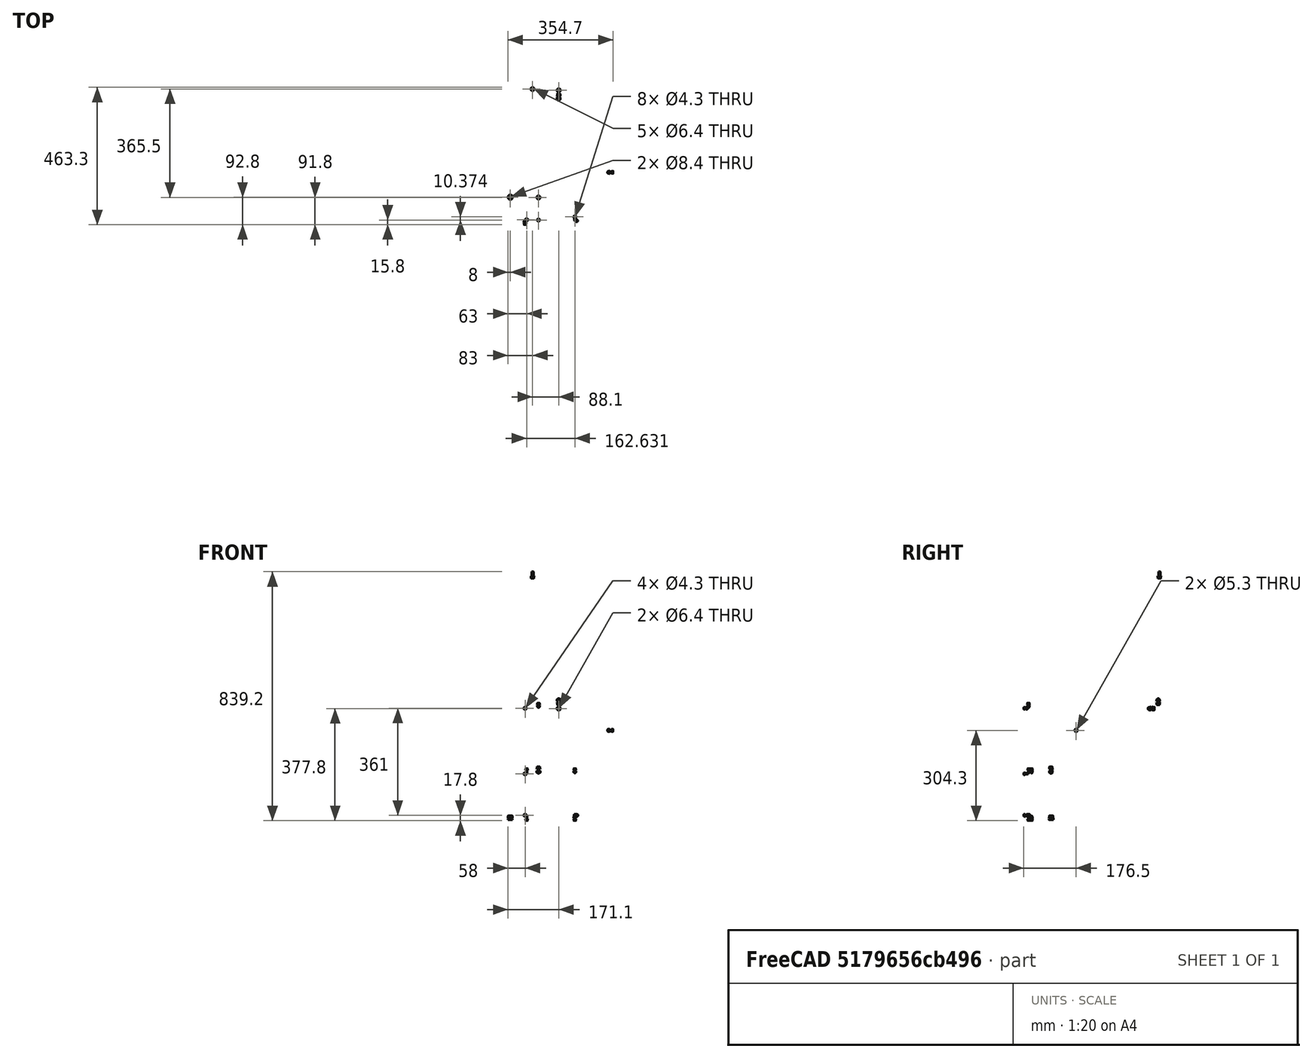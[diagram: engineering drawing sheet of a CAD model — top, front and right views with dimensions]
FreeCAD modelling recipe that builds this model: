
FCSTD DOCUMENT  (FreeCAD 1.0R39319 (Git))
Label: OCT-FRAME-A
License: Creative Commons Attribution 4.0
LicenseURL: https://creativecommons.org/licenses/by/4.0/
objects: App::Link×110, App::LinkElement×90, App::FeaturePython×88, Part::FeaturePython×49, App::Part×27, App::DocumentObjectGroup×16, Assembly::JointGroup×2, Assembly::AssemblyLink×1, Spreadsheet::Sheet×1, Assembly::BomObject×1, Assembly::BomGroup×1, Assembly::AssemblyObject×1
note: 49 computed .brp shape members not serialized (recipe doc carries the construction recipe); baked Part::Feature solids carry a one-line shape summary decoded from their .brp
EXTERNAL_REF file=mechanical RAD/OCT-FRPLB-AA.FCStd obj=Body
EXTERNAL_REF file=mechanical RAD/OCT-CHTOP-AA.FCStd obj=Body
EXTERNAL_REF file=mechanical RAD/OCT-LBRAC-AA.FCStd obj=Body
EXTERNAL_REF file=mechanical RAD/OCT-UBRAC-AA.FCStd obj=Body
EXTERNAL_REF file=mechanical RAD/OCT-FRPLC-AA.FCStd obj=Body
EXTERNAL_REF file=mechanical RAD/OCT-UFPNL.FCStd obj=Body
EXTERNAL_REF file=mechanical RAD/OCT-CPBRC.FCStd obj=Body
EXTERNAL_REF file=mechanical RAD/OCT-UFPNL.FCStd obj=Body002
EXTERNAL_REF file=mechanical RAD/OCT-LBLOK-AB.FCStd obj=Body
EXTERNAL_REF file=mechanical RAD/OCT-ULBLK-AB.FCStd obj=Body
EXTERNAL_REF file=mechanical RAD/OCT-URBLK-AB.FCStd obj=Body
EXTERNAL_REF file=mechanical RAD/OCT-UFPNL.FCStd obj=Body001
EXTERNAL_REF file=mechanical RAD/OCT-CPBRC.FCStd obj=Body002
EXTERNAL_REF file=mechanical COTS/Protex 637DSS Handle Backing Plate Stainless Steel (Natural).FCStd obj=Part__Feature
EXTERNAL_REF file=mechanical RAD/OCT-CHBRA-AC.FCStd obj=Body001
EXTERNAL_REF file=mechanical RAD/OCT-LIDFR-AA.FCStd obj=Body
EXTERNAL_REF file=mechanical COTS/OCT-LDHNG-AA.FCStd obj=Assembly
EXTERNAL_REF file=mechanical COTS/OCT-LDHNG-AA.FCStd obj=outer_half001
EXTERNAL_REF file=mechanical COTS/OCT-LDHNG-AA.FCStd obj=inner_half
EXTERNAL_REF file=mechanical RAD/OCT-LFPNL.FCStd obj=Body002
EXTERNAL_REF file=mechanical RAD/OCT-LFPNL.FCStd obj=Body
EXTERNAL_REF file=mechanical RAD/OCT-LFPNL.FCStd obj=Body003
EXTERNAL_REF file=mechanical COTS/WDS673-82225.FCStd obj=WDS673_82225
EXTERNAL_REF file=mechanical COTS/WDS8520-251.FCStd obj=Part__Feature
EXTERNAL_REF file=mechanical COTS/WDS4213-601.FCStd obj=WDS4213_601

FEATURE [App::Link] Body  label="OCT-FRPLB-AA"
  LinkedObject = -> <external mechanical RAD/OCT-FRPLB-AA.FCStd>#Body
FEATURE [App::FeaturePython] GroundedJoint  label="base plate grounded"  # Assembly grounded joint (typed FeaturePython)
  ObjectToGround = -> Body
FEATURE [App::Link] panel009  label="OCT-CHTOP-AA"
  LinkPlacement = pos=(-3.46e-14,8.68e-14,381) rot=(0,1,0;3.14159rad)
  LinkedObject = -> <external mechanical RAD/OCT-CHTOP-AA.FCStd>#Body
  Placement = pos=(-3.46e-14,8.68e-14,381) rot=(0,1,0;3.14159rad)
FEATURE [App::Link] bracket001  label="OCT-LBRAC-AA"
  LinkPlacement = pos=(149.2,-149.2,4.51e-14) rot=(0,0,1;0.785398rad)
  LinkedObject = -> <external mechanical RAD/OCT-LBRAC-AA.FCStd>#Body
  Placement = pos=(149.2,-149.2,4.51e-14) rot=(0,0,1;0.785398rad)
FEATURE [App::Link] bracket002  label="OCT-LBRAC-AA"
  LinkPlacement = pos=(211,-3.64e-14,3.17e-14) rot=(0,0,1;1.5708rad)
  LinkedObject = -> <external mechanical RAD/OCT-LBRAC-AA.FCStd>#Body
  Placement = pos=(211,-3.64e-14,3.17e-14) rot=(0,0,1;1.5708rad)
FEATURE [App::Link] bracket003  label="OCT-LBRAC-AA"
  LinkPlacement = pos=(149.2,149.2,-4.73e-14) rot=(0,0,1;2.35619rad)
  LinkedObject = -> <external mechanical RAD/OCT-LBRAC-AA.FCStd>#Body
  Placement = pos=(149.2,149.2,-4.73e-14) rot=(0,0,1;2.35619rad)
FEATURE [App::Link] bracket005  label="OCT-LBRAC-AA"
  LinkPlacement = pos=(-149.2,149.2,3.71e-14) rot=(0,0,1;3.92699rad)
  LinkedObject = -> <external mechanical RAD/OCT-LBRAC-AA.FCStd>#Body
  Placement = pos=(-149.2,149.2,3.71e-14) rot=(0,0,1;3.92699rad)
FEATURE [App::Link] bracket006  label="OCT-LBRAC-AA"
  LinkPlacement = pos=(-211,6.19e-14,3.12e-14) rot=(0,0,1;4.71239rad)
  LinkedObject = -> <external mechanical RAD/OCT-LBRAC-AA.FCStd>#Body
  Placement = pos=(-211,6.19e-14,3.12e-14) rot=(0,0,1;4.71239rad)
FEATURE [App::Link] bracket007  label="OCT-LBRAC-AA"
  LinkPlacement = pos=(-149.2,-149.2,4.39e-14) rot=(0,0,-1;0.785398rad)
  LinkedObject = -> <external mechanical RAD/OCT-LBRAC-AA.FCStd>#Body
  Placement = pos=(-149.2,-149.2,4.39e-14) rot=(0,0,-1;0.785398rad)
FEATURE [App::FeaturePython] Joint087  label="lb base 2"  # Assembly joint (typed FeaturePython)
  Activated = true
  AngleMax = 0
  AngleMin = 0
  Detach1 = false
  Detach2 = false
  Distance = 0
  Distance2 = 0
  EnableAngleMax = false
  EnableAngleMin = false
  EnableLengthMax = false
  EnableLengthMin = false
  JointType = 0 (Fixed)
  LengthMax = 0
  LengthMin = 0
  Offset2 = pos=(0,0,0) rot=(0,0,-1;1.5708rad)
  Placement1 = pos=(191.626,-92.631,0) rot=(0,0,1;0.785398rad)
  Placement2 = pos=(70,10,-3.3e-14) rot=(1,0,0;3.14159rad)
  Reference1 = -> Assembly [Body.Edge24,Body.Edge24]
  Reference2 = -> Assembly [bracket001.Edge7,bracket001.Edge7]
FEATURE [App::FeaturePython] Joint089  label="lb base 3"  # Assembly joint (typed FeaturePython)
  Activated = true
  AngleMax = 0
  AngleMin = 0
  Detach1 = false
  Detach2 = false
  Distance = 0
  Distance2 = 0
  EnableAngleMax = false
  EnableAngleMin = false
  EnableLengthMax = false
  EnableLengthMin = false
  JointType = 0 (Fixed)
  LengthMax = 0
  LengthMin = 0
  Offset2 = pos=(0,0,0) rot=(0,0,-1;1.5708rad)
  Placement1 = pos=(201,70,0) rot=(0,0,1;1.5708rad)
  Placement2 = pos=(70,10,-1.96e-14) rot=(1,0,0;3.14159rad)
  Reference1 = -> Assembly [Body.Edge31,Body.Edge31]
  Reference2 = -> Assembly [bracket002.Edge7,bracket002.Edge7]
FEATURE [App::FeaturePython] Joint091  label="lb base 4"  # Assembly joint (typed FeaturePython)
  Activated = true
  AngleMax = 0
  AngleMin = 0
  Detach1 = false
  Detach2 = false
  Distance = 0
  Distance2 = 0
  EnableAngleMax = false
  EnableAngleMin = false
  EnableLengthMax = false
  EnableLengthMin = false
  JointType = 0 (Fixed)
  LengthMax = 0
  LengthMin = 0
  Offset2 = pos=(0,0,0) rot=(0,0,-1;1.5708rad)
  Placement1 = pos=(-70,10,2.86e-14) rot=(0.707107,-0.707107,0;3.14159rad)
  Placement2 = pos=(191.626,92.631,0) rot=(0,0,1;0.785398rad)
  Reference1 = -> Assembly [bracket003.Edge8,bracket003.Edge8]
  Reference2 = -> Assembly [Body.Edge32,Body.Edge32]
FEATURE [App::FeaturePython] Joint095  label="lb base 6"  # Assembly joint (typed FeaturePython)
  Activated = true
  AngleMax = 0
  AngleMin = 0
  Detach1 = false
  Detach2 = false
  Distance = 0
  Distance2 = 0
  EnableAngleMax = false
  EnableAngleMin = false
  EnableLengthMax = false
  EnableLengthMin = false
  JointType = 0 (Fixed)
  LengthMax = 0
  LengthMin = 0
  Offset2 = pos=(0,0,0) rot=(0,0,-1;1.5708rad)
  Placement1 = pos=(70,10,-2.5e-14) rot=(0.707107,-0.707107,0;3.14159rad)
  Placement2 = pos=(-191.626,92.631,0) rot=(0,0,1;2.35619rad)
  Reference1 = -> Assembly [bracket005.Edge7,bracket005.Edge7]
  Reference2 = -> Assembly [Body.Edge27,Body.Edge27]
FEATURE [App::FeaturePython] Joint097  label="lb base 7"  # Assembly joint (typed FeaturePython)
  Activated = true
  AngleMax = 0
  AngleMin = 0
  Detach1 = false
  Detach2 = false
  Distance = 0
  Distance2 = 0
  EnableAngleMax = false
  EnableAngleMin = false
  EnableLengthMax = false
  EnableLengthMin = false
  JointType = 0 (Fixed)
  LengthMax = 0
  LengthMin = 0
  Offset2 = pos=(0,0,0) rot=(0,0,-1;1.5708rad)
  Placement1 = pos=(70,10,-1.91e-14) rot=(0.707107,-0.707107,0;3.14159rad)
  Placement2 = pos=(-201,-70,0) rot=(0,0,-1;3.14159rad)
  Reference1 = -> Assembly [bracket006.Edge7,bracket006.Edge7]
  Reference2 = -> Assembly [Body.Edge20,Body.Edge20]
FEATURE [App::FeaturePython] Joint099  label="lb base 8"  # Assembly joint (typed FeaturePython)
  Activated = true
  AngleMax = 0
  AngleMin = 0
  Detach1 = false
  Detach2 = false
  Distance = 0
  Distance2 = 0
  EnableAngleMax = false
  EnableAngleMin = false
  EnableLengthMax = false
  EnableLengthMin = false
  JointType = 0 (Fixed)
  LengthMax = 0
  LengthMin = 0
  Offset2 = pos=(0,0,0) rot=(0,0,-1;1.5708rad)
  Placement1 = pos=(70,10,-3.18e-14) rot=(-0.707107,0.707107,0;3.14159rad)
  Placement2 = pos=(-92.631,-191.626,0) rot=(0,0,-1;2.35619rad)
  Reference1 = -> Assembly [bracket007.Edge7,bracket007.Edge7]
  Reference2 = -> Assembly [Body.Edge17,Body.Edge17]
FEATURE [App::Link] bracket009  label="OCT-UBRAC-AA"
  LinkPlacement = pos=(149.2,-149.2,160) rot=(0,0,1;0.785398rad)
  LinkedObject = -> <external mechanical RAD/OCT-UBRAC-AA.FCStd>#Body
  Placement = pos=(149.2,-149.2,160) rot=(0,0,1;0.785398rad)
FEATURE [App::Link] bracket011  label="OCT-UBRAC-AA"
  LinkPlacement = pos=(149.2,149.2,160) rot=(0,0,1;2.35619rad)
  LinkedObject = -> <external mechanical RAD/OCT-UBRAC-AA.FCStd>#Body
  Placement = pos=(149.2,149.2,160) rot=(0,0,1;2.35619rad)
FEATURE [App::Link] bracket013  label="OCT-UBRAC-AA"
  LinkPlacement = pos=(-149.2,149.2,160) rot=(0,0,1;3.92699rad)
  LinkedObject = -> <external mechanical RAD/OCT-UBRAC-AA.FCStd>#Body
  Placement = pos=(-149.2,149.2,160) rot=(0,0,1;3.92699rad)
FEATURE [App::Link] bracket014  label="OCT-UBRAC-AA"
  LinkPlacement = pos=(-211,-8.8e-15,160) rot=(0,0,1;4.71239rad)
  LinkedObject = -> <external mechanical RAD/OCT-UBRAC-AA.FCStd>#Body
  Placement = pos=(-211,-8.8e-15,160) rot=(0,0,1;4.71239rad)
FEATURE [App::Link] bracket015  label="OCT-UBRAC-AA"
  LinkPlacement = pos=(-149.2,-149.2,160) rot=(0,0,-1;0.785398rad)
  LinkedObject = -> <external mechanical RAD/OCT-UBRAC-AA.FCStd>#Body
  Placement = pos=(-149.2,-149.2,160) rot=(0,0,-1;0.785398rad)
FEATURE [App::Link] bracket010  label="OCT-UBRAC-AA"
  LinkPlacement = pos=(211,1.342e-13,160) rot=(0,0,1;1.5708rad)
  LinkedObject = -> <external mechanical RAD/OCT-UBRAC-AA.FCStd>#Body
  Placement = pos=(211,1.342e-13,160) rot=(0,0,1;1.5708rad)
FEATURE [App::Link] Body017  label="OCT-FRPLC-AA"
  LinkPlacement = pos=(-2.58e-14,4.22e-14,163) rot=(0,0,1;0rad)
  LinkedObject = -> <external mechanical RAD/OCT-FRPLC-AA.FCStd>#Body
  Placement = pos=(-2.58e-14,4.22e-14,163) rot=(0,0,1;0rad)
FEATURE [App::Link] upper_panel  label="OCT-UFPNL-AB"
  LinkPlacement = pos=(5.7e-15,-211,140) rot=(0,0,1;0rad)
  LinkedObject = -> <external mechanical RAD/OCT-UFPNL.FCStd>#Body
  Placement = pos=(5.7e-15,-211,140) rot=(0,0,1;0rad)
FEATURE [App::Link] upper_panel001  label="OCT-UFPNL-AB"
  LinkPlacement = pos=(149.2,-149.2,140) rot=(0,0,1;0.785398rad)
  LinkedObject = -> <external mechanical RAD/OCT-UFPNL.FCStd>#Body
  Placement = pos=(149.2,-149.2,140) rot=(0,0,1;0.785398rad)
FEATURE [App::Link] upper_panel002  label="OCT-UFPNL-AB"
  LinkPlacement = pos=(149.2,149.2,140) rot=(0,0,1;2.35619rad)
  LinkedObject = -> <external mechanical RAD/OCT-UFPNL.FCStd>#Body
  Placement = pos=(149.2,149.2,140) rot=(0,0,1;2.35619rad)
FEATURE [App::Link] upper_panel003  label="OCT-UFPNL-AB"
  LinkPlacement = pos=(-150.26,150.26,140) rot=(0,0,1;0.785398rad)
  LinkedObject = -> <external mechanical RAD/OCT-UFPNL.FCStd>#Body
  Placement = pos=(-150.26,150.26,140) rot=(0,0,1;0.785398rad)
FEATURE [App::Link] upper_panel004  label="OCT-UFPNL-AB"
  LinkPlacement = pos=(-150.26,-150.26,140) rot=(0,0,1;2.35619rad)
  LinkedObject = -> <external mechanical RAD/OCT-UFPNL.FCStd>#Body
  Placement = pos=(-150.26,-150.26,140) rot=(0,0,1;2.35619rad)
FEATURE [App::Link] chamber_lid_bracket  label="OCT-CPBRC-AA"
  LinkPlacement = pos=(1.419e-13,-211,361) rot=(0,0,1;0rad)
  LinkedObject = -> <external mechanical RAD/OCT-CPBRC.FCStd>#Body
  Placement = pos=(1.419e-13,-211,361) rot=(0,0,1;0rad)
FEATURE [App::Link] chamber_lid_bracket001  label="OCT-CPBRC-AA"
  LinkPlacement = pos=(149.2,-149.2,361) rot=(0,0,1;0.785398rad)
  LinkedObject = -> <external mechanical RAD/OCT-CPBRC.FCStd>#Body
  Placement = pos=(149.2,-149.2,361) rot=(0,0,1;0.785398rad)
FEATURE [App::Link] chamber_lid_bracket002  label="OCT-CPBRC-AA"
  LinkPlacement = pos=(211,2.39e-13,361) rot=(0,0,1;1.5708rad)
  LinkedObject = -> <external mechanical RAD/OCT-CPBRC.FCStd>#Body
  Placement = pos=(211,2.39e-13,361) rot=(0,0,1;1.5708rad)
FEATURE [App::Link] chamber_lid_bracket003  label="OCT-CPBRC-AA"
  LinkPlacement = pos=(149.2,149.2,361) rot=(0,0,1;2.35619rad)
  LinkedObject = -> <external mechanical RAD/OCT-CPBRC.FCStd>#Body
  Placement = pos=(149.2,149.2,361) rot=(0,0,1;2.35619rad)
FEATURE [App::Link] chamber_lid_bracket005  label="OCT-CPBRC-AA"
  LinkPlacement = pos=(-149.2,149.2,361) rot=(0,0,1;3.92699rad)
  LinkedObject = -> <external mechanical RAD/OCT-CPBRC.FCStd>#Body
  Placement = pos=(-149.2,149.2,361) rot=(0,0,1;3.92699rad)
FEATURE [App::Link] chamber_lid_bracket006  label="OCT-CPBRC-AA"
  LinkPlacement = pos=(-211,-1.101e-13,361) rot=(0,0,-1;1.5708rad)
  LinkedObject = -> <external mechanical RAD/OCT-CPBRC.FCStd>#Body
  Placement = pos=(-211,-1.101e-13,361) rot=(0,0,-1;1.5708rad)
FEATURE [App::Link] chamber_lid_bracket007  label="OCT-CPBRC-AA"
  LinkPlacement = pos=(-149.2,-149.2,361) rot=(0,0,-1;0.785398rad)
  LinkedObject = -> <external mechanical RAD/OCT-CPBRC.FCStd>#Body
  Placement = pos=(-149.2,-149.2,361) rot=(0,0,-1;0.785398rad)
FEATURE [App::FeaturePython] Joint147  label="upper panel 2"  # Assembly joint (typed FeaturePython)
  Activated = true
  AngleMax = 0
  AngleMin = 0
  Detach1 = false
  Detach2 = false
  Distance = 0
  Distance2 = 0
  EnableAngleMax = false
  EnableAngleMin = false
  EnableLengthMax = false
  EnableLengthMin = false
  JointType = 0 (Fixed)
  LengthMax = 0
  LengthMin = 0
  Placement1 = pos=(-75,5.68e-14,10) rot=(-1,0,0;1.5708rad)
  Placement2 = pos=(-75,0,-10) rot=(1,0,0;1.5708rad)
  Reference1 = -> Assembly [upper_panel001.Edge12,upper_panel001.Edge12]
  Reference2 = -> Assembly [bracket009.Edge8,bracket009.Edge8]
FEATURE [App::FeaturePython] Joint148  label="upper panel 4"  # Assembly joint (typed FeaturePython)
  Activated = true
  AngleMax = 0
  AngleMin = 0
  Detach1 = false
  Detach2 = false
  Distance = 0
  Distance2 = 0
  EnableAngleMax = false
  EnableAngleMin = false
  EnableLengthMax = false
  EnableLengthMin = false
  JointType = 0 (Fixed)
  LengthMax = 0
  LengthMin = 0
  Placement1 = pos=(-75,0,10) rot=(-1,0,0;1.5708rad)
  Placement2 = pos=(-75,0,-10) rot=(1,0,0;1.5708rad)
  Reference1 = -> Assembly [upper_panel002.Edge12,upper_panel002.Edge12]
  Reference2 = -> Assembly [bracket011.Edge8,bracket011.Edge8]
FEATURE [App::FeaturePython] Joint149  label="upper panel 6"  # Assembly joint (typed FeaturePython)
  Activated = true
  AngleMax = 0
  AngleMin = 0
  Detach1 = false
  Detach2 = false
  Distance = 0
  Distance2 = 0
  EnableAngleMax = false
  EnableAngleMin = false
  EnableLengthMax = false
  EnableLengthMin = false
  JointType = 0 (Fixed)
  LengthMax = 0
  LengthMin = 0
  Offset2 = pos=(0,0,0) rot=(0,0,1;3.14159rad)
  Placement1 = pos=(75,-1.5,10) rot=(1,0,0;1.5708rad)
  Placement2 = pos=(-75,5.68e-14,-10) rot=(0,-0.707107,0.707107;3.14159rad)
  Reference1 = -> Assembly [upper_panel003.Edge27,upper_panel003.Edge27]
  Reference2 = -> Assembly [bracket013.Edge8,bracket013.Edge8]
FEATURE [App::FeaturePython] Joint150  label="upper panel 8"  # Assembly joint (typed FeaturePython)
  Activated = true
  AngleMax = 0
  AngleMin = 0
  Detach1 = false
  Detach2 = false
  Distance = 0
  Distance2 = 0
  EnableAngleMax = false
  EnableAngleMin = false
  EnableLengthMax = false
  EnableLengthMin = false
  JointType = 0 (Fixed)
  LengthMax = 0
  LengthMin = 0
  Offset2 = pos=(0,0,0) rot=(0,0,1;3.14159rad)
  Placement1 = pos=(75,-1.5,10) rot=(1,0,0;1.5708rad)
  Placement2 = pos=(-75,2.84e-14,-10) rot=(0,-0.707107,0.707107;3.14159rad)
  Reference1 = -> Assembly [upper_panel004.Edge27,upper_panel004.Edge27]
  Reference2 = -> Assembly [bracket015.Edge8,bracket015.Edge8]
FEATURE [App::FeaturePython] Joint151  label="upper panel - c bracket 1"  # Assembly joint (typed FeaturePython)
  Activated = true
  AngleMax = 0
  AngleMin = 0
  Detach1 = false
  Detach2 = false
  Distance = 0
  Distance2 = 0
  EnableAngleMax = false
  EnableAngleMin = false
  EnableLengthMax = false
  EnableLengthMin = false
  JointType = 0 (Fixed)
  LengthMax = 0
  LengthMin = 0
  Placement1 = pos=(-75,-2.84e-14,10) rot=(1,0,0;1.5708rad)
  Placement2 = pos=(-75,2.84e-14,231) rot=(-1,0,0;1.5708rad)
  Reference1 = -> Assembly [chamber_lid_bracket.Edge6,chamber_lid_bracket.Edge6]
  Reference2 = -> Assembly [upper_panel.Edge13,upper_panel.Edge13]
FEATURE [App::FeaturePython] Joint152  label="upper panel - c bracket 2"  # Assembly joint (typed FeaturePython)
  Activated = true
  AngleMax = 0
  AngleMin = 0
  Detach1 = false
  Detach2 = false
  Distance = 0
  Distance2 = 0
  EnableAngleMax = false
  EnableAngleMin = false
  EnableLengthMax = false
  EnableLengthMin = false
  JointType = 0 (Fixed)
  LengthMax = 0
  LengthMin = 0
  Placement1 = pos=(-75,0,10) rot=(1,0,0;1.5708rad)
  Placement2 = pos=(-75,5.68e-14,231) rot=(-1,0,0;1.5708rad)
  Reference1 = -> Assembly [chamber_lid_bracket001.Edge6,chamber_lid_bracket001.Edge6]
  Reference2 = -> Assembly [upper_panel001.Edge13,upper_panel001.Edge13]
FEATURE [App::FeaturePython] Joint153  label="upper panel - c bracket 4"  # Assembly joint (typed FeaturePython)
  Activated = true
  AngleMax = 0
  AngleMin = 0
  Detach1 = false
  Detach2 = false
  Distance = 0
  Distance2 = 0
  EnableAngleMax = false
  EnableAngleMin = false
  EnableLengthMax = false
  EnableLengthMin = false
  JointType = 0 (Fixed)
  LengthMax = 0
  LengthMin = 0
  Placement1 = pos=(-75,0,10) rot=(1,0,0;1.5708rad)
  Placement2 = pos=(-75,0,231) rot=(-1,0,0;1.5708rad)
  Reference1 = -> Assembly [chamber_lid_bracket003.Edge6,chamber_lid_bracket003.Edge6]
  Reference2 = -> Assembly [upper_panel002.Edge13,upper_panel002.Edge13]
FEATURE [App::FeaturePython] Joint154  label="upper panel - c bracket 6"  # Assembly joint (typed FeaturePython)
  Activated = true
  AngleMax = 0
  AngleMin = 0
  Detach1 = false
  Detach2 = false
  Distance = 0
  Distance2 = 0
  EnableAngleMax = false
  EnableAngleMin = false
  EnableLengthMax = false
  EnableLengthMin = false
  JointType = 0 (Fixed)
  LengthMax = 0
  LengthMin = 0
  Offset2 = pos=(0,0,0) rot=(0,0,1;3.14159rad)
  Placement1 = pos=(-75,0,10) rot=(1,0,0;1.5708rad)
  Placement2 = pos=(75,-1.5,231) rot=(0,-0.707107,0.707107;3.14159rad)
  Reference1 = -> Assembly [chamber_lid_bracket005.Edge6,chamber_lid_bracket005.Edge6]
  Reference2 = -> Assembly [upper_panel003.Edge28,upper_panel003.Edge28]
FEATURE [App::FeaturePython] Joint155  label="upper panel - c bracket 8"  # Assembly joint (typed FeaturePython)
  Activated = true
  AngleMax = 0
  AngleMin = 0
  Detach1 = false
  Detach2 = false
  Distance = 0
  Distance2 = 0
  EnableAngleMax = false
  EnableAngleMin = false
  EnableLengthMax = false
  EnableLengthMin = false
  JointType = 0 (Fixed)
  LengthMax = 0
  LengthMin = 0
  Offset2 = pos=(0,0,0) rot=(0,0,1;3.14159rad)
  Placement1 = pos=(-75,0,10) rot=(1,0,0;1.5708rad)
  Placement2 = pos=(75,-1.5,231) rot=(0,-0.707107,0.707107;3.14159rad)
  Reference1 = -> Assembly [chamber_lid_bracket007.Edge6,chamber_lid_bracket007.Edge6]
  Reference2 = -> Assembly [upper_panel004.Edge28,upper_panel004.Edge28]
FEATURE [App::FeaturePython] Joint156  label="chamber top - c bracket 1"  # Assembly joint (typed FeaturePython)
  Activated = true
  AngleMax = 0
  AngleMin = 0
  Detach1 = false
  Detach2 = false
  Distance = 0
  Distance2 = 0
  EnableAngleMax = false
  EnableAngleMin = false
  EnableLengthMax = false
  EnableLengthMin = false
  JointType = 0 (Fixed)
  LengthMax = 0
  LengthMin = 0
  Offset2 = pos=(0,0,0) rot=(0,0,1;1.5708rad)
  Placement1 = pos=(30,-202,0) rot=(0,0,1;0rad)
  Placement2 = pos=(-30,9,20) rot=(0,0,1;3.14159rad)
  Reference1 = -> Assembly [panel009.Edge29,panel009.Edge29]
  Reference2 = -> Assembly [chamber_lid_bracket.Edge22,chamber_lid_bracket.Edge22]
FEATURE [App::Link] OCT_UFPNL_CB  label="OCT-UFPNL-CB"
  LinkPlacement = pos=(211,1.6e-14,140) rot=(0,0,1;1.5708rad)
  LinkedObject = -> <external mechanical RAD/OCT-UFPNL.FCStd>#Body002
  Placement = pos=(211,1.6e-14,140) rot=(0,0,1;1.5708rad)
FEATURE [App::FeaturePython] Joint157  label="upper panel - u bracket 3"  # Assembly joint (typed FeaturePython)
  Activated = true
  AngleMax = 0
  AngleMin = 0
  Detach1 = false
  Detach2 = false
  Distance = 0
  Distance2 = 0
  EnableAngleMax = false
  EnableAngleMin = false
  EnableLengthMax = false
  EnableLengthMin = false
  JointType = 0 (Fixed)
  LengthMax = 0
  LengthMin = 0
  Placement1 = pos=(-75,2.84e-14,10) rot=(-1,0,0;1.5708rad)
  Placement2 = pos=(-75,0,-10) rot=(1,0,0;1.5708rad)
  Reference1 = -> Assembly [OCT_UFPNL_CB.Edge12,OCT_UFPNL_CB.Edge12]
  Reference2 = -> Assembly [bracket010.Edge8,bracket010.Edge8]
FEATURE [App::FeaturePython] Joint159  label="upper panel - c bracket 3"  # Assembly joint (typed FeaturePython)
  Activated = true
  AngleMax = 0
  AngleMin = 0
  Detach1 = false
  Detach2 = false
  Distance = 0
  Distance2 = 0
  EnableAngleMax = false
  EnableAngleMin = false
  EnableLengthMax = false
  EnableLengthMin = false
  JointType = 0 (Fixed)
  LengthMax = 0
  LengthMin = 0
  Offset2 = pos=(0,0,0) rot=(0,0,1;1.5708rad)
  Placement1 = pos=(-30,9,20) rot=(0,0,1;1.5708rad)
  Placement2 = pos=(-202,-30,0) rot=(0,0,1;0rad)
  Reference1 = -> Assembly [chamber_lid_bracket002.Edge22,chamber_lid_bracket002.Edge22]
  Reference2 = -> Assembly [panel009.Edge28,panel009.Edge28]
FEATURE [App::FeaturePython] Joint160  label="upper panel - c bracket 7"  # Assembly joint (typed FeaturePython)
  Activated = true
  AngleMax = 0
  AngleMin = 0
  Detach1 = false
  Detach2 = false
  Distance = 0
  Distance2 = 0
  EnableAngleMax = false
  EnableAngleMin = false
  EnableLengthMax = false
  EnableLengthMin = false
  JointType = 0 (Fixed)
  LengthMax = 0
  LengthMin = 0
  Offset2 = pos=(0,0,0) rot=(0,0,1;1.5708rad)
  Placement1 = pos=(-30,9,20) rot=(0,0,1;1.5708rad)
  Placement2 = pos=(202,30,0) rot=(0,0,1;3.14159rad)
  Reference1 = -> Assembly [chamber_lid_bracket006.Edge22,chamber_lid_bracket006.Edge22]
  Reference2 = -> Assembly [panel009.Edge85,panel009.Edge85]
FEATURE [App::Link] lower_block  label="OCT-LBLOK-AB"
  LinkPlacement = pos=(-1.1e-15,-211,0) rot=(0,0,1;0rad)
  LinkedObject = -> <external mechanical RAD/OCT-LBLOK-AB.FCStd>#Body
  Placement = pos=(-1.1e-15,-211,0) rot=(0,0,1;0rad)
FEATURE [App::Link] lower_block001  label="OCT-LBLOK-AB"
  LinkPlacement = pos=(-5.5e-15,-211,20) rot=(0,1,0;3.14159rad)
  LinkedObject = -> <external mechanical RAD/OCT-LBLOK-AB.FCStd>#Body
  Placement = pos=(-5.5e-15,-211,20) rot=(0,1,0;3.14159rad)
FEATURE [App::FeaturePython] Joint161  label="lower block - base FL"  # Assembly joint (typed FeaturePython)
  Activated = true
  AngleMax = 0
  AngleMin = 0
  Detach1 = false
  Detach2 = false
  Distance = 0
  Distance2 = 0
  EnableAngleMax = false
  EnableAngleMin = false
  EnableLengthMax = false
  EnableLengthMin = false
  JointType = 0 (Fixed)
  LengthMax = 0
  LengthMin = 0
  Placement1 = pos=(-70,10,0) rot=(1,0,0;3.14159rad)
  Placement2 = pos=(-70,-201,0) rot=(0,0,1;0rad)
  Reference1 = -> Assembly [lower_block.Edge11,lower_block.Edge11]
  Reference2 = -> Assembly [Body.Edge18,Body.Edge18]
FEATURE [App::FeaturePython] Joint163  label="lower block - base FR"  # Assembly joint (typed FeaturePython)
  Activated = true
  AngleMax = 0
  AngleMin = 0
  Detach1 = false
  Detach2 = false
  Distance = 0
  Distance2 = 0
  EnableAngleMax = false
  EnableAngleMin = false
  EnableLengthMax = false
  EnableLengthMin = false
  JointType = 0 (Fixed)
  LengthMax = 0
  LengthMin = 0
  Offset2 = pos=(0,0,0) rot=(0,0,1;3.14159rad)
  Placement1 = pos=(-70,10,20) rot=(0,0,1;0rad)
  Placement2 = pos=(70,-201,0) rot=(0,0,1;3.14159rad)
  Reference1 = -> Assembly [lower_block001.Edge14,lower_block001.Edge14]
  Reference2 = -> Assembly [Body.Edge21,Body.Edge21]
FEATURE [App::Link] lower_block002  label="OCT-LBLOK-AB"
  LinkPlacement = pos=(5.7e-15,211,20) rot=(1,0,0;3.14159rad)
  LinkedObject = -> <external mechanical RAD/OCT-LBLOK-AB.FCStd>#Body
  Placement = pos=(5.7e-15,211,20) rot=(1,0,0;3.14159rad)
FEATURE [App::Link] lower_block003  label="OCT-LBLOK-AB"
  LinkPlacement = pos=(-7e-16,211,0) rot=(0,0,1;3.14159rad)
  LinkedObject = -> <external mechanical RAD/OCT-LBLOK-AB.FCStd>#Body
  Placement = pos=(-7e-16,211,0) rot=(0,0,1;3.14159rad)
FEATURE [App::FeaturePython] Joint172  label="lower block - base RR"  # Assembly joint (typed FeaturePython)
  Activated = true
  AngleMax = 0
  AngleMin = 0
  Detach1 = false
  Detach2 = false
  Distance = 0
  Distance2 = 0
  EnableAngleMax = false
  EnableAngleMin = false
  EnableLengthMax = false
  EnableLengthMin = false
  JointType = 0 (Fixed)
  LengthMax = 0
  LengthMin = 0
  Offset2 = pos=(0,0,0) rot=(0,0,1;3.14159rad)
  Placement1 = pos=(-70,10,20) rot=(0,0,1;0rad)
  Placement2 = pos=(-70,201,0) rot=(0,0,1;0rad)
  Reference1 = -> Assembly [lower_block002.Edge14,lower_block002.Edge14]
  Reference2 = -> Assembly [Body.Edge30,Body.Edge30]
FEATURE [App::FeaturePython] Joint174  label="lower block - base RL"  # Assembly joint (typed FeaturePython)
  Activated = true
  AngleMax = 0
  AngleMin = 0
  Detach1 = false
  Detach2 = false
  Distance = 0
  Distance2 = 0
  EnableAngleMax = false
  EnableAngleMin = false
  EnableLengthMax = false
  EnableLengthMin = false
  JointType = 0 (Fixed)
  LengthMax = 0
  LengthMin = 0
  Placement1 = pos=(-70,10,0) rot=(1,0,0;3.14159rad)
  Placement2 = pos=(70,201,0) rot=(0,0,1;3.14159rad)
  Reference1 = -> Assembly [lower_block003.Edge11,lower_block003.Edge11]
  Reference2 = -> Assembly [Body.Edge33,Body.Edge33]
FEATURE [App::Link] upper_left_block  label="OCT-ULBLK-AB"
  LinkPlacement = pos=(1.1e-15,-211,120) rot=(0,0,1;0rad)
  LinkedObject = -> <external mechanical RAD/OCT-ULBLK-AB.FCStd>#Body
  Placement = pos=(1.1e-15,-211,120) rot=(0,0,1;0rad)
FEATURE [App::Link] upper_left_block001  label="OCT-ULBLK-AB"
  LinkPlacement = pos=(-3.28e-14,211,120) rot=(0,0,1;3.14159rad)
  LinkedObject = -> <external mechanical RAD/OCT-ULBLK-AB.FCStd>#Body
  Placement = pos=(-3.28e-14,211,120) rot=(0,0,1;3.14159rad)
FEATURE [App::Link] upper_right_block  label="OCT-URBLK-AB"
  LinkPlacement = pos=(3.2e-15,-211,120) rot=(0,0,1;0rad)
  LinkedObject = -> <external mechanical RAD/OCT-URBLK-AB.FCStd>#Body
  Placement = pos=(3.2e-15,-211,120) rot=(0,0,1;0rad)
FEATURE [App::Link] upper_right_block001  label="OCT-URBLK-AB"
  LinkPlacement = pos=(-3.23e-14,211,120) rot=(0,0,1;3.14159rad)
  LinkedObject = -> <external mechanical RAD/OCT-URBLK-AB.FCStd>#Body
  Placement = pos=(-3.23e-14,211,120) rot=(0,0,1;3.14159rad)
FEATURE [App::FeaturePython] Joint176  label="upper panel - u block FL"  # Assembly joint (typed FeaturePython)
  Activated = true
  AngleMax = 0
  AngleMin = 0
  Detach1 = false
  Detach2 = false
  Distance = 0
  Distance2 = 0
  EnableAngleMax = false
  EnableAngleMin = false
  EnableLengthMax = false
  EnableLengthMin = false
  JointType = 0 (Fixed)
  LengthMax = 0
  LengthMin = 0
  Offset2 = pos=(0,0,0) rot=(0,0,1;3.14159rad)
  Placement1 = pos=(-75,0,30) rot=(0,-0.707107,0.707107;3.14159rad)
  Placement2 = pos=(-75,2.84e-14,10) rot=(0,0.707107,0.707107;3.14159rad)
  Reference1 = -> Assembly [upper_left_block.Edge5,upper_left_block.Edge5]
  Reference2 = -> Assembly [upper_panel.Edge12,upper_panel.Edge12]
FEATURE [App::Link] OCT_UFPNL_BB  label="OCT-UFPNL-BB"
  LinkPlacement = pos=(-2.53e-14,212.5,140) rot=(0,0,1;0rad)
  LinkedObject = -> <external mechanical RAD/OCT-UFPNL.FCStd>#Body001
  Placement = pos=(-2.53e-14,212.5,140) rot=(0,0,1;0rad)
FEATURE [App::FeaturePython] Joint180  label="upper panel - u block RL"  # Assembly joint (typed FeaturePython)
  Activated = true
  AngleMax = 0
  AngleMin = 0
  Detach1 = false
  Detach2 = false
  Distance = 0
  Distance2 = 0
  EnableAngleMax = false
  EnableAngleMin = false
  EnableLengthMax = false
  EnableLengthMin = false
  JointType = 0 (Fixed)
  LengthMax = 0
  LengthMin = 0
  Placement1 = pos=(75,-1.5,10) rot=(1,0,0;1.5708rad)
  Placement2 = pos=(-75,0,30) rot=(0,0.707107,-0.707107;3.14159rad)
  Reference1 = -> Assembly [OCT_UFPNL_BB.Edge33,OCT_UFPNL_BB.Edge33]
  Reference2 = -> Assembly [upper_left_block001.Edge5,upper_left_block001.Edge5]
FEATURE [App::Link] OCT_CPBRC_BA  label="OCT-CPBRC-BA"
  LinkPlacement = pos=(3.15e-14,211,361) rot=(0,0,1;3.14159rad)
  LinkedObject = -> <external mechanical RAD/OCT-CPBRC.FCStd>#Body002
  Placement = pos=(3.15e-14,211,361) rot=(0,0,1;3.14159rad)
FEATURE [App::FeaturePython] Joint182  label="upper panel - hinge bracket"  # Assembly joint (typed FeaturePython)
  Activated = true
  AngleMax = 0
  AngleMin = 0
  Detach1 = false
  Detach2 = false
  Distance = 0
  Distance2 = 0
  EnableAngleMax = false
  EnableAngleMin = false
  EnableLengthMax = false
  EnableLengthMin = false
  JointType = 0 (Fixed)
  LengthMax = 0
  LengthMin = 0
  Offset2 = pos=(0,0,0) rot=(0,0,1;3.14159rad)
  Placement1 = pos=(75,-2.84e-14,10) rot=(1,0,0;1.5708rad)
  Placement2 = pos=(-75,-1.5,231) rot=(0,-0.707107,0.707107;3.14159rad)
  Reference1 = -> Assembly [OCT_CPBRC_BA.Edge11,OCT_CPBRC_BA.Edge11]
  Reference2 = -> Assembly [OCT_UFPNL_BB.Edge30,OCT_UFPNL_BB.Edge30]
FEATURE [App::FeaturePython] Joint158  label="upper panel - u bracket 7"  # Assembly joint (typed FeaturePython)
  Activated = true
  AngleMax = 0
  AngleMin = 0
  Detach1 = false
  Detach2 = false
  Distance = 0
  Distance2 = 0
  EnableAngleMax = false
  EnableAngleMin = false
  EnableLengthMax = false
  EnableLengthMin = false
  JointType = 0 (Fixed)
  LengthMax = 0
  LengthMin = 0
  Placement1 = pos=(-75,2.84e-14,10) rot=(-1,0,0;1.5708rad)
  Placement2 = pos=(-75,-2.84e-14,-10) rot=(1,0,0;1.5708rad)
  Reference1 = -> Assembly [OCT_UFPNL_CB001.Edge12,OCT_UFPNL_CB001.Edge12]
  Reference2 = -> Assembly [bracket014.Edge8,bracket014.Edge8]
FEATURE [App::Link] OCT_UFPNL_CB001  label="OCT-UFPNL-CB"
  LinkPlacement = pos=(-211,1.018e-13,140) rot=(0,0,1;4.71239rad)
  LinkedObject = -> <external mechanical RAD/OCT-UFPNL.FCStd>#Body002
  Placement = pos=(-211,1.018e-13,140) rot=(0,0,1;4.71239rad)
FEATURE [App::Link] _37DSS  label="637DSS"
  LinkPlacement = pos=(-209.8,51,252.25) rot=(-0.57735,0.57735,0.57735;4.18879rad)
  LinkedObject = -> <external mechanical COTS/Protex 637DSS Handle Backing Plate Stainless Steel (Natural).FCStd>#Part__Feature
  Placement = pos=(-209.8,51,252.25) rot=(-0.57735,0.57735,0.57735;4.18879rad)
FEATURE [App::Link] _37DSS001  label="637DSS"
  LinkPlacement = pos=(209.8,-51,252.25) rot=(0.57735,0.57735,0.57735;2.0944rad)
  LinkedObject = -> <external mechanical COTS/Protex 637DSS Handle Backing Plate Stainless Steel (Natural).FCStd>#Part__Feature
  Placement = pos=(209.8,-51,252.25) rot=(0.57735,0.57735,0.57735;2.0944rad)
FEATURE [App::FeaturePython] Joint185  label="left handle backing block"  # Assembly joint (typed FeaturePython)
  Activated = true
  AngleMax = 0
  AngleMin = 0
  Detach1 = false
  Detach2 = false
  Distance = 0
  Distance2 = 0
  EnableAngleMax = false
  EnableAngleMin = false
  EnableLengthMax = false
  EnableLengthMin = false
  JointType = 0 (Fixed)
  LengthMax = 0
  LengthMin = 0
  Offset2 = pos=(0,0,0) rot=(0,0,1;3.14159rad)
  Placement1 = pos=(9.7,44.25,1.2) rot=(-1,0,0;3.14159rad)
  Placement2 = pos=(-41.3,2.84e-14,156.5) rot=(-1,0,0;1.5708rad)
  Reference1 = -> Assembly [_37DSS.Edge38,_37DSS.Edge38]
  Reference2 = -> Assembly [OCT_UFPNL_CB001.Edge14,OCT_UFPNL_CB001.Edge14]
FEATURE [App::FeaturePython] Joint186  label="right handle backing block"  # Assembly joint (typed FeaturePython)
  Activated = true
  AngleMax = 0
  AngleMin = 0
  Detach1 = false
  Detach2 = false
  Distance = 0
  Distance2 = 0
  EnableAngleMax = false
  EnableAngleMin = false
  EnableLengthMax = false
  EnableLengthMin = false
  JointType = 0 (Fixed)
  LengthMax = 0
  LengthMin = 0
  Offset2 = pos=(0,0,0) rot=(0,0,1;3.14159rad)
  Placement1 = pos=(9.7,44.25,1.2) rot=(1,0,0;3.14159rad)
  Placement2 = pos=(-41.3,2.84e-14,156.5) rot=(-1,0,0;1.5708rad)
  Reference1 = -> Assembly [_37DSS001.Edge38,_37DSS001.Edge38]
  Reference2 = -> Assembly [OCT_UFPNL_CB.Edge14,OCT_UFPNL_CB.Edge14]
FEATURE [App::Link] brace  label="OCT-CHBRA-AC"
  LinkPlacement = pos=(-1.1e-14,-111,163) rot=(0,0,1;0rad)
  LinkedObject = -> <external mechanical RAD/OCT-CHBRA-AC.FCStd>#Body001
  Placement = pos=(-1.1e-14,-111,163) rot=(0,0,1;0rad)
FEATURE [App::Link] brace001  label="OCT-CHBRA-AC"
  LinkPlacement = pos=(78.4889,-78.4889,163) rot=(0,0,1;0.785398rad)
  LinkedObject = -> <external mechanical RAD/OCT-CHBRA-AC.FCStd>#Body001
  Placement = pos=(78.4889,-78.4889,163) rot=(0,0,1;0.785398rad)
FEATURE [App::Link] brace002  label="OCT-CHBRA-AC"
  LinkPlacement = pos=(111,7.03e-14,163) rot=(0,0,1;1.5708rad)
  LinkedObject = -> <external mechanical RAD/OCT-CHBRA-AC.FCStd>#Body001
  Placement = pos=(111,7.03e-14,163) rot=(0,0,1;1.5708rad)
FEATURE [App::Link] brace003  label="OCT-CHBRA-AC"
  LinkPlacement = pos=(78.4889,78.4889,163) rot=(0,0,1;2.35619rad)
  LinkedObject = -> <external mechanical RAD/OCT-CHBRA-AC.FCStd>#Body001
  Placement = pos=(78.4889,78.4889,163) rot=(0,0,1;2.35619rad)
FEATURE [App::Link] brace004  label="OCT-CHBRA-AC"
  LinkPlacement = pos=(-3.89e-14,111,163) rot=(0,0,1;3.14159rad)
  LinkedObject = -> <external mechanical RAD/OCT-CHBRA-AC.FCStd>#Body001
  Placement = pos=(-3.89e-14,111,163) rot=(0,0,1;3.14159rad)
FEATURE [App::Link] brace005  label="OCT-CHBRA-AC"
  LinkPlacement = pos=(-78.4889,78.4889,163) rot=(0,0,1;3.92699rad)
  LinkedObject = -> <external mechanical RAD/OCT-CHBRA-AC.FCStd>#Body001
  Placement = pos=(-78.4889,78.4889,163) rot=(0,0,1;3.92699rad)
FEATURE [App::Link] brace006  label="OCT-CHBRA-AC"
  LinkPlacement = pos=(-111,3.51e-14,163) rot=(0,0,-1;1.5708rad)
  LinkedObject = -> <external mechanical RAD/OCT-CHBRA-AC.FCStd>#Body001
  Placement = pos=(-111,3.51e-14,163) rot=(0,0,-1;1.5708rad)
FEATURE [App::Link] brace007  label="OCT-CHBRA-AC"
  LinkPlacement = pos=(-78.4889,-78.4889,163) rot=(0,0,-1;0.785398rad)
  LinkedObject = -> <external mechanical RAD/OCT-CHBRA-AC.FCStd>#Body001
  Placement = pos=(-78.4889,-78.4889,163) rot=(0,0,-1;0.785398rad)
FEATURE [Part::FeaturePython] Washer022  label="M6-Washer"  # WARN: FeaturePython — macro-defined, semantics opaque (R4)
  Diameter = 7
  Invert = false
  MatchOuter = false
  OffsetAngle = 0
  Placement = pos=(38.1,215.5,370) rot=(-1,0,0;1.5708rad)
  Type = 8
FEATURE [Part::FeaturePython] Screw013  label="M6x16-Screw"  # WARN: FeaturePython — macro-defined, semantics opaque (R4)
  BaseObject = -> Washer022 [Edge1]
  Diameter = 7
  Invert = false
  LeftHanded = false
  Length = 4
  LengthCustom = 16
  MatchOuter = false
  OffsetAngle = 0
  Placement = pos=(38.1,217.1,370) rot=(-1,0,0;1.5708rad)
  Thread = false
  Type = 75
FEATURE [Part::FeaturePython] Washer023  label="M6-Washer"  # WARN: FeaturePython — macro-defined, semantics opaque (R4)
  BaseObject = -> OCT_UFPNL_BB [Hole001.Edge35]
  Diameter = 7
  Invert = false
  MatchOuter = false
  OffsetAngle = 0
  Placement = pos=(38.1,211,370) rot=(1,0,0;1.5708rad)
  Type = 8
FEATURE [Part::FeaturePython] Nut009  label="M6-Nut"  # WARN: FeaturePython — macro-defined, semantics opaque (R4)
  BaseObject = -> Washer023 [Edge1]
  Diameter = 8
  Invert = false
  LeftHanded = false
  MatchOuter = false
  OffsetAngle = 0
  Placement = pos=(38.1,209.4,370) rot=(1,0,0;1.5708rad)
  Thread = false
  Type = 31
FEATURE [App::Part] Part001  label="hinge lower fasteners"
  Group = -> [Washer023,Nut009,Washer022,Screw013]
  Origin = -> Origin014
FEATURE [App::Link] hinge_fastener_group  label="hinge lower fastener set"
  LinkPlacement = pos=(-331.9,1.527e-13,408.1) rot=(0,1,0;1.5708rad)
  LinkedObject = -> Part001
  Placement = pos=(-331.9,1.527e-13,408.1) rot=(0,1,0;1.5708rad)
FEATURE [App::Link] hinge_fastener_group001  label="hinge lower fastener set"
  LinkPlacement = pos=(-357.3,1.733e-13,399.6) rot=(0,1,0;1.5708rad)
  LinkedObject = -> Part001
  Placement = pos=(-357.3,1.733e-13,399.6) rot=(0,1,0;1.5708rad)
FEATURE [App::Link] hinge_fastener_group002  label="hinge lower fastener set"
  LinkPlacement = pos=(-382.7,1.757e-13,399.6) rot=(0,1,0;1.5708rad)
  LinkedObject = -> Part001
  Placement = pos=(-382.7,1.757e-13,399.6) rot=(0,1,0;1.5708rad)
FEATURE [App::Link] hinge_fastener_group003  label="hinge lower fastener set"
  LinkPlacement = pos=(-408.1,1.73e-13,408.1) rot=(0,1,0;1.5708rad)
  LinkedObject = -> Part001
  Placement = pos=(-408.1,1.73e-13,408.1) rot=(0,1,0;1.5708rad)
FEATURE [Part::FeaturePython] Washer024  label="M6-Washer"  # WARN: FeaturePython — macro-defined, semantics opaque (R4)
  Diameter = 7
  Invert = true
  MatchOuter = false
  OffsetAngle = 0
  Placement = pos=(-50,239.5,817) rot=(0.363166,-0.931725,0;3.14159rad)
  Type = 8
FEATURE [Part::FeaturePython] Screw014  label="M6x16-Screw"  # WARN: FeaturePython — macro-defined, semantics opaque (R4)
  BaseObject = -> Washer024 [Edge1]
  Diameter = 7
  Invert = false
  LeftHanded = false
  Length = 4
  LengthCustom = 16
  MatchOuter = false
  OffsetAngle = 0
  Placement = pos=(-50,239.5,815.4) rot=(-1,0,0;3.14159rad)
  Thread = false
  Type = 75
FEATURE [App::Part] Part002  label="lid handle fasteners"
  Group = -> [Washer024,Screw014]
  Origin = -> Origin015
FEATURE [App::Link] lid_handle_fastener_group  label="lid handle fastener group"
  LinkPlacement = pos=(-175.268,29.3379,-1.48384e-11) rot=(0,0,-1;0.743326rad)
  LinkedObject = -> Part002
  Placement = pos=(-175.268,29.3379,-1.48384e-11) rot=(0,0,-1;0.743326rad)
FEATURE [App::Link] lid_handle_fastener_group001  label="lid handle fastener group"
  LinkPlacement = pos=(-75.2683,29.3379,-1.4849e-11) rot=(0,0,-1;0.743326rad)
  LinkedObject = -> Part002
  Placement = pos=(-75.2683,29.3379,-1.4849e-11) rot=(0,0,-1;0.743326rad)
FEATURE [App::Link] lid_frame  label="lid frame"
  LinkPlacement = pos=(-2.141e-12,289.5,606) rot=(-1,0,0;1.5708rad)
  LinkedObject = -> <external mechanical RAD/OCT-LIDFR-AA.FCStd>#Body
  Placement = pos=(-2.141e-12,289.5,606) rot=(-1,0,0;1.5708rad)
FEATURE [Part::FeaturePython] Washer025  label="M6-Washer"  # WARN: FeaturePython — macro-defined, semantics opaque (R4)
  Diameter = 7
  Invert = false
  MatchOuter = false
  OffsetAngle = 0
  Placement = pos=(38.1,235.5,390) rot=(-0.939424,-0.342757,0;3.14159rad)
  Type = 8
FEATURE [Part::FeaturePython] Screw015  label="M6x16-Screw"  # WARN: FeaturePython — macro-defined, semantics opaque (R4)
  BaseObject = -> Washer025 [Edge1]
  Diameter = 7
  Invert = false
  LeftHanded = false
  Length = 4
  LengthCustom = 16
  MatchOuter = false
  OffsetAngle = 0
  Placement = pos=(38.1,235.5,388.4) rot=(-1,0,0;3.14159rad)
  Thread = false
  Type = 75
FEATURE [Part::FeaturePython] Washer026  label="M6-Washer"  # WARN: FeaturePython — macro-defined, semantics opaque (R4)
  Diameter = 7
  Invert = false
  MatchOuter = false
  Offset = 2
  OffsetAngle = 0
  Placement = pos=(38.1,235.5,395) rot=(0,0,1;0rad)
  Type = 8
FEATURE [Part::FeaturePython] Nut010  label="M6-Nut"  # WARN: FeaturePython — macro-defined, semantics opaque (R4)
  BaseObject = -> Washer026 [Edge1]
  Diameter = 8
  Invert = false
  LeftHanded = false
  MatchOuter = false
  OffsetAngle = 0
  Placement = pos=(38.1,235.5,396.6) rot=(0,0,1;0rad)
  Thread = false
  Type = 31
FEATURE [App::Part] Part003  label="hinge upper fasteners"
  Group = -> [Washer025,Screw015,Washer026,Nut010]
  Origin = -> Origin016
FEATURE [App::Link] hinge_upper_fasteners  label="hinge upper fasteners"
  LinkPlacement = pos=(218.907,391.13,-4.423e-13) rot=(0,0,1;2.44189rad)
  LinkedObject = -> Part003
  Placement = pos=(218.907,391.13,-4.423e-13) rot=(0,0,1;2.44189rad)
FEATURE [App::Link] hinge_upper_fasteners001  label="hinge upper fasteners"
  LinkPlacement = pos=(193.507,399.63,-4.268e-13) rot=(0,0,1;2.44189rad)
  LinkedObject = -> Part003
  Placement = pos=(193.507,399.63,-4.268e-13) rot=(0,0,1;2.44189rad)
FEATURE [App::Link] hinge_upper_fasteners002  label="hinge upper fasteners"
  LinkPlacement = pos=(168.107,399.63,-4.597e-13) rot=(0,0,1;2.44189rad)
  LinkedObject = -> Part003
  Placement = pos=(168.107,399.63,-4.597e-13) rot=(0,0,1;2.44189rad)
FEATURE [App::Link] hinge_upper_fasteners003  label="hinge upper fasteners"
  LinkPlacement = pos=(142.707,391.13,-4.27e-13) rot=(0,0,1;2.44189rad)
  LinkedObject = -> Part003
  Placement = pos=(142.707,391.13,-4.27e-13) rot=(0,0,1;2.44189rad)
FEATURE [App::FeaturePython] Joint219  label="left lid handle fastener"  # Assembly joint (typed FeaturePython)
  Activated = true
  AngleMax = 0
  AngleMin = 0
  Detach1 = false
  Detach2 = false
  Distance = 0
  Distance2 = 0
  EnableAngleMax = false
  EnableAngleMin = false
  EnableLengthMax = false
  EnableLengthMin = false
  JointType = 0 (Fixed)
  LengthMax = 0
  LengthMin = 0
  Placement2 = pos=(-50,-211,-50) rot=(0,0.707107,-0.707107;3.14159rad)
  Reference1 = -> Assembly [lid_handle_fastener_group.Washer024.Edge3,lid_handle_fastener_group.Washer024.Edge3]
  Reference2 = -> Assembly [lid_frame.Edge237,lid_frame.Edge237]
FEATURE [App::FeaturePython] Joint220  label="right lid handl fastener"  # Assembly joint (typed FeaturePython)
  Activated = true
  AngleMax = 0
  AngleMin = 0
  Detach1 = false
  Detach2 = false
  Distance = 0
  Distance2 = 0
  EnableAngleMax = false
  EnableAngleMin = false
  EnableLengthMax = false
  EnableLengthMin = false
  JointType = 0 (Fixed)
  LengthMax = 0
  LengthMin = 0
  Placement2 = pos=(50,-211,-50) rot=(0,0.707107,-0.707107;3.14159rad)
  Reference1 = -> Assembly [lid_handle_fastener_group001.Washer024.Edge3,lid_handle_fastener_group001.Washer024.Edge3]
  Reference2 = -> Assembly [lid_frame.Edge238,lid_frame.Edge238]
FEATURE [App::Link] outer_half001  label="outer half"
  LinkPlacement = pos=(-51,216.5,389) rot=(-0.57735,0.57735,0.57735;2.0944rad)
  LinkedObject = -> <external mechanical COTS/OCT-LDHNG-AA.FCStd>#outer_half001
  Placement = pos=(-51,216.5,389) rot=(-0.57735,0.57735,0.57735;2.0944rad)
FEATURE [App::Link] inner_half001  label="inner half"
  LinkPlacement = pos=(-51,216.5,389) rot=(-0.57735,0.57735,0.57735;2.0944rad)
  LinkedObject = -> <external mechanical COTS/OCT-LDHNG-AA.FCStd>#inner_half
  Placement = pos=(-51,216.5,389) rot=(-0.57735,0.57735,0.57735;2.0944rad)
FEATURE [App::FeaturePython] Joint222  label="hinge - upper panel"  # Assembly joint (typed FeaturePython)
  Activated = true
  AngleMax = 0
  AngleMin = 0
  Detach1 = false
  Detach2 = false
  Distance = 0
  Distance2 = 0
  EnableAngleMax = false
  EnableAngleMin = false
  EnableLengthMax = false
  EnableLengthMin = false
  JointType = 0 (Fixed)
  LengthMax = 0
  LengthMin = 0
  Offset2 = pos=(0,0,0) rot=(0,0,-1;1.5708rad)
  Placement1 = pos=(19,-89.1,-4) rot=(-1,0,0;3.14159rad)
  Placement2 = pos=(38.1,2.84e-14,230) rot=(-0.57735,0.57735,0.57735;2.0944rad)
  Reference1 = -> Assembly [OCT_LDHNG_AA.outer_half001.Edge20,OCT_LDHNG_AA.outer_half001.Edge20]
  Reference2 = -> Assembly [OCT_UFPNL_BB.Edge18,OCT_UFPNL_BB.Edge18]
FEATURE [App::FeaturePython] Joint223  label="lower hinge fastener 1"  # Assembly joint (typed FeaturePython)
  Activated = true
  AngleMax = 0
  AngleMin = 0
  Detach1 = false
  Detach2 = false
  Distance = 0
  Distance2 = 0
  EnableAngleMax = false
  EnableAngleMin = false
  EnableLengthMax = false
  EnableLengthMin = false
  JointType = 0 (Fixed)
  LengthMax = 0
  LengthMin = 0
  Placement2 = pos=(19,-89.1,-1) rot=(0,0,1;0rad)
  Reference1 = -> Assembly [hinge_fastener_group.Washer022.Edge3,hinge_fastener_group.Washer022.Edge3]
  Reference2 = -> Assembly [OCT_LDHNG_AA.outer_half001.Edge41,OCT_LDHNG_AA.outer_half001.Edge41]
FEATURE [App::FeaturePython] Joint224  label="lower hinge fastener 2"  # Assembly joint (typed FeaturePython)
  Activated = true
  AngleMax = 0
  AngleMin = 0
  Detach1 = false
  Detach2 = false
  Distance = 0
  Distance2 = 0
  EnableAngleMax = false
  EnableAngleMin = false
  EnableLengthMax = false
  EnableLengthMin = false
  JointType = 0 (Fixed)
  LengthMax = 0
  LengthMin = 0
  Placement1 = pos=(27.5,-63.7,-1) rot=(0,0,1;0rad)
  Reference1 = -> Assembly [OCT_LDHNG_AA.outer_half001.Edge42,OCT_LDHNG_AA.outer_half001.Edge42]
  Reference2 = -> Assembly [hinge_fastener_group001.Washer022.Edge3,hinge_fastener_group001.Washer022.Edge3]
FEATURE [App::FeaturePython] Joint225  label="lower hinge fastener 3"  # Assembly joint (typed FeaturePython)
  Activated = true
  AngleMax = 0
  AngleMin = 0
  Detach1 = false
  Detach2 = false
  Distance = 0
  Distance2 = 0
  EnableAngleMax = false
  EnableAngleMin = false
  EnableLengthMax = false
  EnableLengthMin = false
  JointType = 0 (Fixed)
  LengthMax = 0
  LengthMin = 0
  Placement2 = pos=(27.5,-38.3,-1) rot=(0,0,1;0rad)
  Reference1 = -> Assembly [hinge_fastener_group002.Washer022.Edge3,hinge_fastener_group002.Washer022.Edge3]
  Reference2 = -> Assembly [OCT_LDHNG_AA.outer_half001.Edge44,OCT_LDHNG_AA.outer_half001.Edge44]
FEATURE [App::FeaturePython] Joint226  label="lower hinge fastener 4"  # Assembly joint (typed FeaturePython)
  Activated = true
  AngleMax = 0
  AngleMin = 0
  Detach1 = false
  Detach2 = false
  Distance = 0
  Distance2 = 0
  EnableAngleMax = false
  EnableAngleMin = false
  EnableLengthMax = false
  EnableLengthMin = false
  JointType = 0 (Fixed)
  LengthMax = 0
  LengthMin = 0
  Placement2 = pos=(19,-12.9,-1) rot=(0,0,1;0rad)
  Reference1 = -> Assembly [hinge_fastener_group003.Washer022.Edge3,hinge_fastener_group003.Washer022.Edge3]
  Reference2 = -> Assembly [OCT_LDHNG_AA.outer_half001.Edge43,OCT_LDHNG_AA.outer_half001.Edge43]
FEATURE [App::FeaturePython] Joint227  label="hinge - lid frame"  # Assembly joint (typed FeaturePython)
  Activated = true
  AngleMax = 0
  AngleMin = 0
  Detach1 = false
  Detach2 = false
  Distance = 0
  Distance2 = 0
  EnableAngleMax = false
  EnableAngleMin = false
  EnableLengthMax = false
  EnableLengthMin = false
  JointType = 0 (Fixed)
  LengthMax = 0
  LengthMin = 0
  Offset1 = pos=(0,2,0) rot=(0,0,1;0rad)
  Placement1 = pos=(38.1,213,-54) rot=(0,-0.707107,-0.707107;3.14159rad)
  Placement2 = pos=(-4,-89.1,19) rot=(-0.57735,-0.57735,0.57735;2.0944rad)
  Reference1 = -> Assembly [lid_frame.Edge85,lid_frame.Edge85]
  Reference2 = -> Assembly [OCT_LDHNG_AA.inner_half001.Edge72,OCT_LDHNG_AA.inner_half001.Edge72]
FEATURE [App::FeaturePython] Joint228  label="upper hinge fastener 1"  # Assembly joint (typed FeaturePython)
  Activated = true
  AngleMax = 0
  AngleMin = 0
  Detach1 = false
  Detach2 = false
  Distance = 0
  Distance2 = 0
  EnableAngleMax = false
  EnableAngleMin = false
  EnableLengthMax = false
  EnableLengthMin = false
  JointType = 0 (Fixed)
  LengthMax = 0
  LengthMin = 0
  Placement2 = pos=(-1,-89.1,19) rot=(0.57735,0.57735,0.57735;2.0944rad)
  Reference1 = -> Assembly [hinge_upper_fasteners.Washer025.Edge5,hinge_upper_fasteners.Washer025.Edge5]
  Reference2 = -> Assembly [OCT_LDHNG_AA.inner_half001.Edge15,OCT_LDHNG_AA.inner_half001.Edge15]
FEATURE [App::FeaturePython] Joint229  label="upper hinge fastener 2"  # Assembly joint (typed FeaturePython)
  Activated = true
  AngleMax = 0
  AngleMin = 0
  Detach1 = false
  Detach2 = false
  Distance = 0
  Distance2 = 0
  EnableAngleMax = false
  EnableAngleMin = false
  EnableLengthMax = false
  EnableLengthMin = false
  JointType = 0 (Fixed)
  LengthMax = 0
  LengthMin = 0
  Placement2 = pos=(-1,-63.7,27.5) rot=(0.57735,0.57735,0.57735;2.0944rad)
  Reference1 = -> Assembly [hinge_upper_fasteners001.Washer025.Edge3,hinge_upper_fasteners001.Washer025.Edge3]
  Reference2 = -> Assembly [OCT_LDHNG_AA.inner_half001.Edge16,OCT_LDHNG_AA.inner_half001.Edge16]
FEATURE [App::FeaturePython] Joint230  label="upper hinge fastener 3"  # Assembly joint (typed FeaturePython)
  Activated = true
  AngleMax = 0
  AngleMin = 0
  Detach1 = false
  Detach2 = false
  Distance = 0
  Distance2 = 0
  EnableAngleMax = false
  EnableAngleMin = false
  EnableLengthMax = false
  EnableLengthMin = false
  JointType = 0 (Fixed)
  LengthMax = 0
  LengthMin = 0
  Placement2 = pos=(-1,-38.3,27.5) rot=(0.57735,0.57735,0.57735;2.0944rad)
  Reference1 = -> Assembly [hinge_upper_fasteners002.Washer025.Edge3,hinge_upper_fasteners002.Washer025.Edge3]
  Reference2 = -> Assembly [OCT_LDHNG_AA.inner_half001.Edge18,OCT_LDHNG_AA.inner_half001.Edge18]
FEATURE [App::FeaturePython] Joint231  label="upper hinge fastener 4"  # Assembly joint (typed FeaturePython)
  Activated = true
  AngleMax = 0
  AngleMin = 0
  Detach1 = false
  Detach2 = false
  Distance = 0
  Distance2 = 0
  EnableAngleMax = false
  EnableAngleMin = false
  EnableLengthMax = false
  EnableLengthMin = false
  JointType = 0 (Fixed)
  LengthMax = 0
  LengthMin = 0
  Placement2 = pos=(-1,-12.9,19) rot=(0.57735,0.57735,0.57735;2.0944rad)
  Reference1 = -> Assembly [hinge_upper_fasteners003.Washer025.Edge3,hinge_upper_fasteners003.Washer025.Edge3]
  Reference2 = -> Assembly [OCT_LDHNG_AA.inner_half001.Edge17,OCT_LDHNG_AA.inner_half001.Edge17]
FEATURE [App::FeaturePython] Joint232  label="Revolute"  # Assembly joint (typed FeaturePython)
  Activated = true
  AngleMax = 90
  AngleMin = 0
  Detach1 = false
  Detach2 = false
  Distance = 0
  Distance2 = 0
  EnableAngleMax = true
  EnableAngleMin = true
  EnableLengthMax = false
  EnableLengthMin = false
  JointType = 1 (Revolute)
  LengthMax = 0
  LengthMin = 0
  Placement1 = pos=(0,-59.75,0) rot=(-1,0,0;1.5708rad)
  Placement2 = pos=(0,-59.75,0) rot=(-1,0,0;1.5708rad)
  Reference1 = -> Assembly [OCT_LDHNG_AA.inner_half001.Edge61,OCT_LDHNG_AA.inner_half001.Edge61]
  Reference2 = -> Assembly [OCT_LDHNG_AA.outer_half001.Edge69,OCT_LDHNG_AA.outer_half001.Edge69]
FEATURE [Assembly::JointGroup] Joints001
  Group = -> [Joint232]
FEATURE [Assembly::AssemblyLink] OCT_LDHNG_AA  label="OCT-LDHNG-AA"
  Group = -> [Joints001,outer_half001,inner_half001,Joint232]
  LinkedObject = -> <external mechanical COTS/OCT-LDHNG-AA.FCStd>#Assembly
  Origin = -> Origin017
  Rigid = false
FEATURE [App::Link] OCT_LFPNL_BA  label="OCT-LFPNL-BA"
  LinkPlacement = pos=(9.3e-15,-213,70) rot=(0,0,1;0rad)
  LinkedObject = -> <external mechanical RAD/OCT-LFPNL.FCStd>#Body002
  Placement = pos=(9.3e-15,-213,70) rot=(0,0,1;0rad)
FEATURE [App::FeaturePython] Joint  label="front lower panel"  # Assembly joint (typed FeaturePython)
  Activated = true
  AngleMax = 0
  AngleMin = 0
  Detach1 = false
  Detach2 = false
  Distance = 0
  Distance2 = 0
  EnableAngleMax = false
  EnableAngleMin = false
  EnableLengthMax = false
  EnableLengthMin = false
  JointType = 0 (Fixed)
  LengthMax = 0
  LengthMin = 0
  Offset2 = pos=(0,0,0) rot=(0,0,1;3.14159rad)
  Placement1 = pos=(-75,0,10) rot=(0,-0.707107,0.707107;3.14159rad)
  Placement2 = pos=(-75,2,-60) rot=(0,0.707107,0.707107;3.14159rad)
  Reference1 = -> Assembly [lower_block.Edge5,lower_block.Edge5]
  Reference2 = -> Assembly [OCT_LFPNL_BA.Edge37,OCT_LFPNL_BA.Edge37]
FEATURE [App::Link] OCT_LFPNL_AB  label="OCT-LFPNL-AB"
  LinkPlacement = pos=(150.614,-150.614,70) rot=(0,0,1;0.785398rad)
  LinkedObject = -> <external mechanical RAD/OCT-LFPNL.FCStd>#Body
  Placement = pos=(150.614,-150.614,70) rot=(0,0,1;0.785398rad)
FEATURE [App::Link] OCT_LFPNL_AB001  label="OCT-LFPNL-AB"
  LinkPlacement = pos=(213,-1.397e-13,70) rot=(0,0,1;1.5708rad)
  LinkedObject = -> <external mechanical RAD/OCT-LFPNL.FCStd>#Body
  Placement = pos=(213,-1.397e-13,70) rot=(0,0,1;1.5708rad)
FEATURE [App::Link] OCT_LFPNL_AB002  label="OCT-LFPNL-AB"
  LinkPlacement = pos=(150.614,150.614,70) rot=(0,0,1;2.35619rad)
  LinkedObject = -> <external mechanical RAD/OCT-LFPNL.FCStd>#Body
  Placement = pos=(150.614,150.614,70) rot=(0,0,1;2.35619rad)
FEATURE [App::FeaturePython] Joint233  label="base lower panel 1"  # Assembly joint (typed FeaturePython)
  Activated = true
  AngleMax = 0
  AngleMin = 0
  Detach1 = false
  Detach2 = false
  Distance = 0
  Distance2 = 0
  EnableAngleMax = false
  EnableAngleMin = false
  EnableLengthMax = false
  EnableLengthMin = false
  JointType = 0 (Fixed)
  LengthMax = 0
  LengthMin = 0
  Placement1 = pos=(-75,2,-60) rot=(-1,0,0;1.5708rad)
  Placement2 = pos=(-75,0,10) rot=(1,0,0;1.5708rad)
  Reference1 = -> Assembly [OCT_LFPNL_AB.Edge25,OCT_LFPNL_AB.Edge25]
  Reference2 = -> Assembly [bracket001.Edge26,bracket001.Edge26]
FEATURE [App::FeaturePython] Joint234  label="base lower panel 2"  # Assembly joint (typed FeaturePython)
  Activated = true
  AngleMax = 0
  AngleMin = 0
  Detach1 = false
  Detach2 = false
  Distance = 0
  Distance2 = 0
  EnableAngleMax = false
  EnableAngleMin = false
  EnableLengthMax = false
  EnableLengthMin = false
  JointType = 0 (Fixed)
  LengthMax = 0
  LengthMin = 0
  Placement1 = pos=(-75,2,-60) rot=(-1,0,0;1.5708rad)
  Placement2 = pos=(-75,-2.84e-14,10) rot=(1,0,0;1.5708rad)
  Reference1 = -> Assembly [OCT_LFPNL_AB001.Edge25,OCT_LFPNL_AB001.Edge25]
  Reference2 = -> Assembly [bracket002.Edge26,bracket002.Edge26]
FEATURE [App::FeaturePython] Joint235  label="base lower panel 3"  # Assembly joint (typed FeaturePython)
  Activated = true
  AngleMax = 0
  AngleMin = 0
  Detach1 = false
  Detach2 = false
  Distance = 0
  Distance2 = 0
  EnableAngleMax = false
  EnableAngleMin = false
  EnableLengthMax = false
  EnableLengthMin = false
  JointType = 0 (Fixed)
  LengthMax = 0
  LengthMin = 0
  Placement1 = pos=(-75,2,-60) rot=(-1,0,0;1.5708rad)
  Placement2 = pos=(-75,-2.84e-14,10) rot=(1,0,0;1.5708rad)
  Reference1 = -> Assembly [OCT_LFPNL_AB002.Edge25,OCT_LFPNL_AB002.Edge25]
  Reference2 = -> Assembly [bracket003.Edge26,bracket003.Edge26]
FEATURE [App::Link] OCT_LFPNL_CA  label="OCT-LFPNL-CA"
  LinkPlacement = pos=(-1.91e-14,213,70) rot=(0,0,1;3.14159rad)
  LinkedObject = -> <external mechanical RAD/OCT-LFPNL.FCStd>#Body003
  Placement = pos=(-1.91e-14,213,70) rot=(0,0,1;3.14159rad)
FEATURE [App::Link] OCT_LFPNL_AB003  label="OCT-LFPNL-AB"
  LinkPlacement = pos=(-149.2,149.2,70) rot=(0,0,1;0.785398rad)
  LinkedObject = -> <external mechanical RAD/OCT-LFPNL.FCStd>#Body
  Placement = pos=(-149.2,149.2,70) rot=(0,0,1;0.785398rad)
FEATURE [App::Link] OCT_LFPNL_AB004  label="OCT-LFPNL-AB"
  LinkPlacement = pos=(-211,1.509e-13,70) rot=(0,0,1;1.5708rad)
  LinkedObject = -> <external mechanical RAD/OCT-LFPNL.FCStd>#Body
  Placement = pos=(-211,1.509e-13,70) rot=(0,0,1;1.5708rad)
FEATURE [App::Link] OCT_LFPNL_AB005  label="OCT-LFPNL-AB"
  LinkPlacement = pos=(-149.2,-149.2,70) rot=(0,0,1;2.35619rad)
  LinkedObject = -> <external mechanical RAD/OCT-LFPNL.FCStd>#Body
  Placement = pos=(-149.2,-149.2,70) rot=(0,0,1;2.35619rad)
FEATURE [App::FeaturePython] Joint236  label="lower PSU panel"  # Assembly joint (typed FeaturePython)
  Activated = true
  AngleMax = 0
  AngleMin = 0
  Detach1 = false
  Detach2 = false
  Distance = 0
  Distance2 = 0
  EnableAngleMax = false
  EnableAngleMin = false
  EnableLengthMax = false
  EnableLengthMin = false
  JointType = 0 (Fixed)
  LengthMax = 0
  LengthMin = 0
  Offset2 = pos=(0,0,0) rot=(0,0,1;3.14159rad)
  Placement1 = pos=(-75,2,-60) rot=(1,0,0;4.71239rad)
  Placement2 = pos=(-75,0,10) rot=(1,0,0;1.5708rad)
  Reference1 = -> Assembly [OCT_LFPNL_CA.Edge118,OCT_LFPNL_CA.Edge118]
  Reference2 = -> Assembly [lower_block003.Edge5,lower_block003.Edge5]
FEATURE [App::FeaturePython] Joint237  label="base lower panel 4"  # Assembly joint (typed FeaturePython)
  Activated = true
  AngleMax = 0
  AngleMin = 0
  Detach1 = false
  Detach2 = false
  Distance = 0
  Distance2 = 0
  EnableAngleMax = false
  EnableAngleMin = false
  EnableLengthMax = false
  EnableLengthMin = false
  JointType = 0 (Fixed)
  LengthMax = 0
  LengthMin = 0
  Offset2 = pos=(0,0,0) rot=(0,0,1;3.14159rad)
  Placement1 = pos=(75,0,-60) rot=(1,0,0;1.5708rad)
  Placement2 = pos=(-75,0,10) rot=(0,-0.707107,0.707107;3.14159rad)
  Reference1 = -> Assembly [OCT_LFPNL_AB003.Edge14,OCT_LFPNL_AB003.Edge14]
  Reference2 = -> Assembly [bracket005.Edge26,bracket005.Edge26]
FEATURE [App::FeaturePython] Joint238  label="base lower panel 5"  # Assembly joint (typed FeaturePython)
  Activated = true
  AngleMax = 0
  AngleMin = 0
  Detach1 = false
  Detach2 = false
  Distance = 0
  Distance2 = 0
  EnableAngleMax = false
  EnableAngleMin = false
  EnableLengthMax = false
  EnableLengthMin = false
  JointType = 0 (Fixed)
  LengthMax = 0
  LengthMin = 0
  Offset2 = pos=(0,0,0) rot=(0,0,1;3.14159rad)
  Placement1 = pos=(75,-2.84e-14,-60) rot=(1,0,0;1.5708rad)
  Placement2 = pos=(-75,-2.84e-14,10) rot=(0,-0.707107,0.707107;3.14159rad)
  Reference1 = -> Assembly [OCT_LFPNL_AB004.Edge14,OCT_LFPNL_AB004.Edge14]
  Reference2 = -> Assembly [bracket006.Edge26,bracket006.Edge26]
FEATURE [App::FeaturePython] Joint239  label="base lower panel 6"  # Assembly joint (typed FeaturePython)
  Activated = true
  AngleMax = 0
  AngleMin = 0
  Detach1 = false
  Detach2 = false
  Distance = 0
  Distance2 = 0
  EnableAngleMax = false
  EnableAngleMin = false
  EnableLengthMax = false
  EnableLengthMin = false
  JointType = 0 (Fixed)
  LengthMax = 0
  LengthMin = 0
  Offset2 = pos=(0,0,0) rot=(0,0,1;3.14159rad)
  Placement1 = pos=(-75,0,10) rot=(1,0,0;1.5708rad)
  Placement2 = pos=(75,-2.84e-14,-60) rot=(0,-0.707107,0.707107;3.14159rad)
  Reference1 = -> Assembly [bracket007.Edge26,bracket007.Edge26]
  Reference2 = -> Assembly [OCT_LFPNL_AB005.Edge14,OCT_LFPNL_AB005.Edge14]
FEATURE [App::FeaturePython] Joint240  label="rear left upper block"  # Assembly joint (typed FeaturePython)
  Activated = true
  AngleMax = 0
  AngleMin = 0
  Detach1 = false
  Detach2 = false
  Distance = 0
  Distance2 = 0
  EnableAngleMax = false
  EnableAngleMin = false
  EnableLengthMax = false
  EnableLengthMin = false
  JointType = 0 (Fixed)
  LengthMax = 0
  LengthMin = 0
  Offset2 = pos=(0,0,0) rot=(0,0,1;3.14159rad)
  Placement1 = pos=(-75,0,10) rot=(0,0.707107,-0.707107;3.14159rad)
  Placement2 = pos=(-75,2,60) rot=(0,-0.707107,-0.707107;3.14159rad)
  Reference1 = -> Assembly [upper_left_block001.Edge6,upper_left_block001.Edge6]
  Reference2 = -> Assembly [OCT_LFPNL_CA.Edge122,OCT_LFPNL_CA.Edge122]
FEATURE [App::DocumentObjectGroup] Group  label="Lower panels"
  Group = -> [OCT_LFPNL_AB005,OCT_LFPNL_AB004,OCT_LFPNL_AB003,OCT_LFPNL_CA,OCT_LFPNL_AB002,OCT_LFPNL_AB001,OCT_LFPNL_AB,OCT_LFPNL_BA]
FEATURE [App::DocumentObjectGroup] Group001  label="Hinge"
  Group = -> [hinge_upper_fasteners003,hinge_upper_fasteners002,hinge_upper_fasteners001,hinge_upper_fasteners,hinge_fastener_group,hinge_fastener_group001,hinge_fastener_group002,hinge_fastener_group003,OCT_LDHNG_AA]
FEATURE [App::DocumentObjectGroup] Group004  label="Lower brackets"
  Group = -> [lower_block,lower_block001,lower_block002,lower_block003,bracket001,bracket002,bracket003,bracket005,bracket006,bracket007]
FEATURE [App::DocumentObjectGroup] Group005  label="Chamber Braces"
  Group = -> [brace,brace001,brace002,brace003,brace004,brace005,brace006,brace007]
FEATURE [App::DocumentObjectGroup] Group006  label="Upper panels"
  Group = -> [upper_panel,upper_panel001,upper_panel002,upper_panel003,upper_panel004,OCT_UFPNL_CB,OCT_UFPNL_CB001,OCT_UFPNL_BB]
FEATURE [App::DocumentObjectGroup] Group007  label="Top Brackets"
  Group = -> [chamber_lid_bracket002,chamber_lid_bracket003,chamber_lid_bracket005,chamber_lid_bracket006,chamber_lid_bracket007,OCT_CPBRC_BA,chamber_lid_bracket001,chamber_lid_bracket]
FEATURE [App::DocumentObjectGroup] Group008  label="Upper brackets"
  Group = -> [bracket009,bracket010,bracket011,bracket013,bracket014,bracket015,upper_left_block,upper_left_block001,upper_right_block,upper_right_block001]
FEATURE [App::DocumentObjectGroup] Group010  label="Plates"
  Group = -> [Body,Body017,panel009]
FEATURE [Part::FeaturePython] Washer027  label="M4-Washer"  # WARN: FeaturePython — macro-defined, semantics opaque (R4)
  BaseObject = -> OCT_LFPNL_AB [Chamfer.Edge12]
  Diameter = 5
  Invert = false
  MatchOuter = false
  OffsetAngle = 0
  Placement = pos=(97.5807,-203.647,10) rot=(0.707107,0.707107,0;1.5708rad)
  Type = 8
FEATURE [Part::FeaturePython] Screw016  label="M4x10-Screw"  # WARN: FeaturePython — macro-defined, semantics opaque (R4)
  BaseObject = -> Washer027 [Edge1]
  Diameter = 5
  Invert = false
  LeftHanded = false
  Length = 2
  LengthCustom = 10
  MatchOuter = false
  OffsetAngle = 0
  Placement = pos=(98.1464,-204.212,10) rot=(0.707107,0.707107,0;1.5708rad)
  Thread = false
  Type = 75
FEATURE [Part::FeaturePython] Washer028  label="M4-Washer"  # WARN: FeaturePython — macro-defined, semantics opaque (R4)
  BaseObject = -> bracket001 [Mirrored.Edge34]
  Diameter = 5
  Invert = false
  MatchOuter = false
  OffsetAngle = 0
  Placement = pos=(95.1059,-201.172,10) rot=(-0.707107,-0.707107,0;1.5708rad)
  Type = 8
FEATURE [Part::FeaturePython] Nut011  label="M4-Nut"  # WARN: FeaturePython — macro-defined, semantics opaque (R4)
  BaseObject = -> Washer028 [Edge1]
  Diameter = 6
  Invert = false
  LeftHanded = false
  MatchOuter = false
  OffsetAngle = 0
  Placement = pos=(94.5402,-200.606,10) rot=(-0.707107,-0.707107,0;1.5708rad)
  Thread = false
  Type = 31
FEATURE [Part::FeaturePython] Washer029  label="M4-Washer"  # WARN: FeaturePython — macro-defined, semantics opaque (R4)
  BaseObject = -> OCT_LFPNL_BA [Pocket.Edge12]
  Diameter = 5
  Invert = false
  MatchOuter = false
  OffsetAngle = 0
  Placement = pos=(-75,-213,10) rot=(1,0,0;1.5708rad)
  Type = 8
FEATURE [Part::FeaturePython] Screw017  label="M4x10-Screw"  # WARN: FeaturePython — macro-defined, semantics opaque (R4)
  BaseObject = -> Washer029 [Edge1]
  Diameter = 5
  Invert = false
  LeftHanded = false
  Length = 2
  LengthCustom = 10
  MatchOuter = false
  OffsetAngle = 0
  Placement = pos=(-75,-213.8,10) rot=(1,0,0;1.5708rad)
  Thread = false
  Type = 75
FEATURE [Part::FeaturePython] Washer032  label="M4-Washer"  # WARN: FeaturePython — macro-defined, semantics opaque (R4)
  BaseObject = -> Body [Hole001.Edge43]
  Diameter = 5
  Invert = false
  MatchOuter = false
  OffsetAngle = 0
  Placement = pos=(-70,-201,-3) rot=(-1,0,0;3.14159rad)
  Type = 8
FEATURE [Part::FeaturePython] Screw019  label="M4x12-Screw"  # WARN: FeaturePython — macro-defined, semantics opaque (R4)
  BaseObject = -> Washer032 [Edge1]
  Diameter = 5
  Invert = false
  LeftHanded = false
  Length = 3
  LengthCustom = 12
  MatchOuter = false
  OffsetAngle = 0
  Placement = pos=(-70,-201,-3.8) rot=(-1,0,0;3.14159rad)
  Thread = false
  Type = 75
FEATURE [App::LinkElement] Link_i0
  LinkedObject = -> Part008
  _LinkOwner = 4673
FEATURE [App::LinkElement] Link_i1
  LinkPlacement = pos=(1,0,0) rot=(0,0,1;0.670245rad)
  LinkedObject = -> Part008
  Placement = pos=(1,0,0) rot=(0,0,1;0.670245rad)
  _LinkOwner = 4673
FEATURE [App::Link] Link  label="baseplate single side"
  ElementCount = 2
  ElementList = -> [Link_i0,Link_i1]
  LinkedObject = -> Part008
FEATURE [App::LinkElement] Link001_i0
  LinkedObject = -> Link
  _LinkOwner = 4682
FEATURE [App::LinkElement] Link001_i1
  LinkPlacement = pos=(0,0,0) rot=(0,0,1;0.785398rad)
  LinkedObject = -> Link
  Placement = pos=(0,0,0) rot=(0,0,1;0.785398rad)
  _LinkOwner = 4682
FEATURE [App::LinkElement] Link001_i2
  LinkPlacement = pos=(0,0,0) rot=(0,0,1;1.5708rad)
  LinkedObject = -> Link
  Placement = pos=(0,0,0) rot=(0,0,1;1.5708rad)
  _LinkOwner = 4682
FEATURE [App::LinkElement] Link001_i3
  LinkPlacement = pos=(0,0,0) rot=(0,0,1;3.14159rad)
  LinkedObject = -> Link
  Placement = pos=(0,0,0) rot=(0,0,1;3.14159rad)
  _LinkOwner = 4682
FEATURE [App::LinkElement] Link001_i4
  LinkPlacement = pos=(0,0,0) rot=(0,0,1;3.92699rad)
  LinkedObject = -> Link
  Placement = pos=(0,0,0) rot=(0,0,1;3.92699rad)
  _LinkOwner = 4682
FEATURE [App::LinkElement] Link001_i5
  LinkPlacement = pos=(0,0,0) rot=(0,0,1;4.71239rad)
  LinkedObject = -> Link
  Placement = pos=(0,0,0) rot=(0,0,1;4.71239rad)
  _LinkOwner = 4682
FEATURE [App::Link] Link001  label="baseplate all sides"
  ElementCount = 6
  ElementList = -> [Link001_i0,Link001_i1,Link001_i2,Link001_i3,Link001_i4,Link001_i5]
  LinkedObject = -> Link
FEATURE [Part::FeaturePython] Washer034  label="M4-Washer"  # WARN: FeaturePython — macro-defined, semantics opaque (R4)
  BaseObject = -> Body [Hole001.Edge47]
  Diameter = 5
  Invert = false
  MatchOuter = true
  OffsetAngle = 0
  Placement = pos=(92.631,-191.626,-3) rot=(-1,0,0;3.14159rad)
  Type = 8
FEATURE [Part::FeaturePython] Washer035  label="M4-Washer"  # WARN: FeaturePython — macro-defined, semantics opaque (R4)
  BaseObject = -> Washer034 [Edge3]
  Diameter = 5
  Invert = true
  MatchOuter = true
  Offset = 4.5
  OffsetAngle = 0
  Placement = pos=(92.631,-191.626,1.5) rot=(0,0,1;0rad)
  Type = 8
FEATURE [App::DocumentObjectGroup] Group014  label="Washers"
  Group = -> [Washer034,Washer035]
FEATURE [Part::FeaturePython] Screw020  label="M4x12-Screw"  # WARN: FeaturePython — macro-defined, semantics opaque (R4)
  BaseObject = -> Washer034 [Edge1]
  Diameter = 5
  Invert = false
  LeftHanded = false
  Length = 3
  LengthCustom = 12
  MatchOuter = true
  OffsetAngle = 0
  Placement = pos=(92.631,-191.626,-3.8) rot=(-1,0,0;3.14159rad)
  Thread = false
  Type = 75
FEATURE [App::DocumentObjectGroup] Group015  label="Screws"
  Group = -> [Screw020]
FEATURE [Part::FeaturePython] Nut013  label="M4-Nut"  # WARN: FeaturePython — macro-defined, semantics opaque (R4)
  BaseObject = -> Washer035 [Edge1]
  Diameter = 6
  Invert = false
  LeftHanded = false
  MatchOuter = true
  OffsetAngle = 0
  Placement = pos=(92.631,-191.626,2.3) rot=(0,0,1;0rad)
  Thread = false
  Type = 31
FEATURE [App::DocumentObjectGroup] Group016  label="Nuts"
  Group = -> [Nut013]
FEATURE [App::Part] Part008  label="base plate bracket fastener single"
  Group = -> [Group014,Washer034,Washer035,Group015,Group016,Nut013,Screw020]
  Origin = -> Origin022
FEATURE [App::Part] Part009  label="baseplate bracket fasteners"
  Group = -> [Part008,Link,Link001]
  Origin = -> Origin023
FEATURE [App::Part] Part010  label="baseplate block single fastener"
  Group = -> [Washer032,Screw019]
  Origin = -> Origin024
FEATURE [App::LinkElement] Link002_i0
  LinkedObject = -> Part010
  _LinkOwner = 4719
FEATURE [App::LinkElement] Link002_i1
  LinkPlacement = pos=(0,0,0) rot=(0,0,1;0.670245rad)
  LinkedObject = -> Part010
  Placement = pos=(0,0,0) rot=(0,0,1;0.670245rad)
  _LinkOwner = 4719
FEATURE [App::Link] Link002  label="baseplate single side"
  ElementCount = 2
  ElementList = -> [Link002_i0,Link002_i1]
  LinkedObject = -> Part010
FEATURE [App::LinkElement] Link003_i0
  LinkedObject = -> Link002
  _LinkOwner = 4722
FEATURE [App::LinkElement] Link003_i1
  LinkPlacement = pos=(0,0,0) rot=(0,0,1;3.14159rad)
  LinkedObject = -> Link002
  Placement = pos=(0,0,0) rot=(0,0,1;3.14159rad)
  _LinkOwner = 4722
FEATURE [App::Link] Link003  label="baseplate both sides"
  ElementCount = 2
  ElementList = -> [Link003_i0,Link003_i1]
  LinkedObject = -> Link002
FEATURE [App::Part] Part007  label="baseplate block fasteners"
  Group = -> [Part010,Link002,Link003]
  Origin = -> Origin021
FEATURE [App::Part] Part011  label="lower panel block single"
  Group = -> [Screw017,Washer029]
  Origin = -> Origin025
FEATURE [App::LinkElement] Link004_i0
  LinkedObject = -> Part011
  _LinkOwner = 4734
FEATURE [App::LinkElement] Link004_i1
  LinkPlacement = pos=(150,0,0) rot=(0,0,1;0rad)
  LinkedObject = -> Part011
  Placement = pos=(150,0,0) rot=(0,0,1;0rad)
  _LinkOwner = 4734
FEATURE [App::LinkElement] Link004_i2
  LinkPlacement = pos=(0,0,120) rot=(0,0,1;0rad)
  LinkedObject = -> Part011
  Placement = pos=(0,0,120) rot=(0,0,1;0rad)
  _LinkOwner = 4734
FEATURE [App::LinkElement] Link004_i3
  LinkPlacement = pos=(150,0,120) rot=(0,0,1;0rad)
  LinkedObject = -> Part011
  Placement = pos=(150,0,120) rot=(0,0,1;0rad)
  _LinkOwner = 4734
FEATURE [App::Link] Link004  label="lower panel block one panel"
  ElementCount = 4
  ElementList = -> [Link004_i0,Link004_i1,Link004_i2,Link004_i3]
  LinkedObject = -> Part011
FEATURE [App::LinkElement] Link005_i0
  LinkedObject = -> Link004
  _LinkOwner = 4739
FEATURE [App::LinkElement] Link005_i1
  LinkPlacement = pos=(0,0,0) rot=(0,0,1;3.14159rad)
  LinkedObject = -> Link004
  Placement = pos=(0,0,0) rot=(0,0,1;3.14159rad)
  _LinkOwner = 4739
FEATURE [App::Link] Link005  label="lower panel all blocks"
  ElementCount = 2
  ElementList = -> [Link005_i0,Link005_i1]
  LinkedObject = -> Link004
FEATURE [App::Part] Part005  label="lower panel block fasteners"
  Group = -> [Part011,Link004,Link005]
  Origin = -> Origin019
FEATURE [App::Part] Part012  label="single fastener"
  Group = -> [Nut011,Washer028,Screw016,Washer027]
  Origin = -> Origin026
FEATURE [App::LinkElement] Link006_i0
  LinkedObject = -> Part012
  _LinkOwner = 4754
FEATURE [App::LinkElement] Link006_i1
  LinkPlacement = pos=(106.066,106.066,0) rot=(0,0,1;0rad)
  LinkedObject = -> Part012
  Placement = pos=(106.066,106.066,0) rot=(0,0,1;0rad)
  _LinkOwner = 4754
FEATURE [App::LinkElement] Link006_i2
  LinkPlacement = pos=(0,0,120) rot=(0,0,1;0rad)
  LinkedObject = -> Part012
  Placement = pos=(0,0,120) rot=(0,0,1;0rad)
  _LinkOwner = 4754
FEATURE [App::LinkElement] Link006_i3
  LinkPlacement = pos=(106.066,106.066,120) rot=(0,0,1;0rad)
  LinkedObject = -> Part012
  Placement = pos=(106.066,106.066,120) rot=(0,0,1;0rad)
  _LinkOwner = 4754
FEATURE [App::Link] Link006  label="single panel"
  ElementCount = 4
  ElementList = -> [Link006_i0,Link006_i1,Link006_i2,Link006_i3]
  LinkedObject = -> Part012
FEATURE [App::LinkElement] Link007_i0
  LinkedObject = -> Link006
  _LinkOwner = 4759
FEATURE [App::LinkElement] Link007_i1
  LinkPlacement = pos=(0,0,0) rot=(0,0,1;0.785398rad)
  LinkedObject = -> Link006
  Placement = pos=(0,0,0) rot=(0,0,1;0.785398rad)
  _LinkOwner = 4759
FEATURE [App::LinkElement] Link007_i2
  LinkPlacement = pos=(0,0,0) rot=(0,0,1;1.5708rad)
  LinkedObject = -> Link006
  Placement = pos=(0,0,0) rot=(0,0,1;1.5708rad)
  _LinkOwner = 4759
FEATURE [App::LinkElement] Link007_i3
  LinkPlacement = pos=(0,0,0) rot=(0,0,1;3.14159rad)
  LinkedObject = -> Link006
  Placement = pos=(0,0,0) rot=(0,0,1;3.14159rad)
  _LinkOwner = 4759
FEATURE [App::LinkElement] Link007_i4
  LinkPlacement = pos=(0,0,0) rot=(0,0,1;3.92699rad)
  LinkedObject = -> Link006
  Placement = pos=(0,0,0) rot=(0,0,1;3.92699rad)
  _LinkOwner = 4759
FEATURE [App::LinkElement] Link007_i5
  LinkPlacement = pos=(0,0,0) rot=(0,0,1;4.71239rad)
  LinkedObject = -> Link006
  Placement = pos=(0,0,0) rot=(0,0,1;4.71239rad)
  _LinkOwner = 4759
FEATURE [App::Link] Link007  label="all panels"
  ElementCount = 6
  ElementList = -> [Link007_i0,Link007_i1,Link007_i2,Link007_i3,Link007_i4,Link007_i5]
  LinkedObject = -> Link006
FEATURE [App::Part] Part004  label="lower panel bracket fasteners"
  Group = -> [Part012,Link006,Link007]
  Origin = -> Origin018
FEATURE [Part::FeaturePython] Washer036  label="M4-Washer"  # WARN: FeaturePython — macro-defined, semantics opaque (R4)
  BaseObject = -> upper_panel [Chamfer.Edge25]
  Diameter = 5
  Invert = false
  MatchOuter = true
  OffsetAngle = 0
  Placement = pos=(-75,-212.5,150) rot=(1,0,0;1.5708rad)
  Type = 8
FEATURE [Part::FeaturePython] Screw021  label="M4x10-Screw"  # WARN: FeaturePython — macro-defined, semantics opaque (R4)
  BaseObject = -> Washer036 [Edge1]
  Diameter = 5
  Invert = false
  LeftHanded = false
  Length = 2
  LengthCustom = 10
  MatchOuter = true
  OffsetAngle = 0
  Placement = pos=(-75,-213.3,150) rot=(1,0,0;1.5708rad)
  Thread = false
  Type = 75
FEATURE [App::Part] Part014  label="single fastener"
  Group = -> [Screw021,Washer036]
  Origin = -> Origin028
FEATURE [App::LinkElement] Link008_i0
  LinkedObject = -> Part014
  _LinkOwner = 4784
FEATURE [App::LinkElement] Link008_i1
  LinkPlacement = pos=(150,0,0) rot=(0,0,1;0rad)
  LinkedObject = -> Part014
  Placement = pos=(150,0,0) rot=(0,0,1;0rad)
  _LinkOwner = 4784
FEATURE [App::LinkElement] Link008_i2
  LinkPlacement = pos=(0,0,0) rot=(0,0,1;3.14159rad)
  LinkedObject = -> Part014
  Placement = pos=(0,0,0) rot=(0,0,1;3.14159rad)
  _LinkOwner = 4784
FEATURE [App::LinkElement] Link008_i3
  LinkPlacement = pos=(-150,0,0) rot=(0,0,1;3.14159rad)
  LinkedObject = -> Part014
  Placement = pos=(-150,0,0) rot=(0,0,1;3.14159rad)
  _LinkOwner = 4784
FEATURE [App::Link] Link008  label="all panels"
  ElementCount = 4
  ElementList = -> [Link008_i0,Link008_i1,Link008_i2,Link008_i3]
  LinkedObject = -> Part014
FEATURE [App::Part] Part013  label="upper panel block fasteners"
  Group = -> [Part014,Link008]
  Origin = -> Origin027
FEATURE [Part::FeaturePython] Washer037  label="M4-Washer"  # WARN: FeaturePython — macro-defined, semantics opaque (R4)
  BaseObject = -> Body017 [Hole001.Edge10]
  Diameter = 5
  Invert = false
  MatchOuter = true
  OffsetAngle = 0
  Placement = pos=(-70,-201,163) rot=(0,0,1;0rad)
  Type = 8
FEATURE [Part::FeaturePython] Screw022  label="M4x12-Screw"  # WARN: FeaturePython — macro-defined, semantics opaque (R4)
  BaseObject = -> Washer037 [Edge1]
  Diameter = 5
  Invert = false
  LeftHanded = false
  Length = 3
  LengthCustom = 12
  MatchOuter = true
  OffsetAngle = 0
  Placement = pos=(-70,-201,163.8) rot=(0,0,1;0rad)
  Thread = false
  Type = 75
FEATURE [App::Part] Part016  label="single fastener"
  Group = -> [Screw022,Washer037]
  Origin = -> Origin030
FEATURE [App::LinkElement] Link009_i0
  LinkedObject = -> Part016
  _LinkOwner = 4810
FEATURE [App::LinkElement] Link009_i1
  LinkPlacement = pos=(140,0,0) rot=(0,0,1;0rad)
  LinkedObject = -> Part016
  Placement = pos=(140,0,0) rot=(0,0,1;0rad)
  _LinkOwner = 4810
FEATURE [App::LinkElement] Link009_i2
  LinkPlacement = pos=(0,402,0) rot=(0,0,1;0rad)
  LinkedObject = -> Part016
  Placement = pos=(0,402,0) rot=(0,0,1;0rad)
  _LinkOwner = 4810
FEATURE [App::LinkElement] Link009_i3
  LinkPlacement = pos=(140,402,0) rot=(0,0,1;0rad)
  LinkedObject = -> Part016
  Placement = pos=(140,402,0) rot=(0,0,1;0rad)
  _LinkOwner = 4810
FEATURE [App::Link] Link009  label="pattern"
  ElementCount = 4
  ElementList = -> [Link009_i0,Link009_i1,Link009_i2,Link009_i3]
  LinkedObject = -> Part016
FEATURE [App::Part] Part015  label="mid plate block fasteners"
  Group = -> [Part016,Link009]
  Origin = -> Origin029
FEATURE [Part::FeaturePython] Washer038  label="M4-Washer"  # WARN: FeaturePython — macro-defined, semantics opaque (R4)
  BaseObject = -> Body017 [Hole001.Edge31]
  Diameter = 5
  Invert = false
  MatchOuter = true
  OffsetAngle = 0
  Placement = pos=(92.631,-191.626,163) rot=(0,0,1;0rad)
  Type = 8
FEATURE [Part::FeaturePython] Screw023  label="M4x12-Screw"  # WARN: FeaturePython — macro-defined, semantics opaque (R4)
  BaseObject = -> Washer038 [Edge1]
  Diameter = 5
  Invert = false
  LeftHanded = false
  Length = 3
  LengthCustom = 12
  MatchOuter = true
  OffsetAngle = 0
  Placement = pos=(92.631,-191.626,163.8) rot=(0,0,1;0rad)
  Thread = false
  Type = 75
FEATURE [Part::FeaturePython] Washer039  label="M4-Washer"  # WARN: FeaturePython — macro-defined, semantics opaque (R4)
  BaseObject = -> bracket009 [Mirrored.Edge39]
  Diameter = 5
  Invert = false
  MatchOuter = true
  OffsetAngle = 0
  Placement = pos=(92.631,-191.626,158.5) rot=(-1,0,0;3.14159rad)
  Type = 8
FEATURE [Part::FeaturePython] Nut014  label="M4-Nut"  # WARN: FeaturePython — macro-defined, semantics opaque (R4)
  BaseObject = -> Washer039 [Edge1]
  Diameter = 6
  Invert = false
  LeftHanded = false
  MatchOuter = true
  OffsetAngle = 0
  Placement = pos=(92.631,-191.626,157.7) rot=(-1,0,0;3.14159rad)
  Thread = false
  Type = 31
FEATURE [App::Part] Part018  label="single fastener"
  Group = -> [Nut014,Washer039,Screw023,Washer038]
  Origin = -> Origin032
FEATURE [App::LinkElement] Link010_i0
  LinkedObject = -> Part018
  _LinkOwner = 4835
FEATURE [App::LinkElement] Link010_i1
  LinkPlacement = pos=(98.9949,98.9949,0) rot=(0,0,1;0rad)
  LinkedObject = -> Part018
  Placement = pos=(98.9949,98.9949,0) rot=(0,0,1;0rad)
  _LinkOwner = 4835
FEATURE [App::Link] Link010  label="single bracket"
  ElementCount = 2
  ElementList = -> [Link010_i0,Link010_i1]
  LinkedObject = -> Part018
FEATURE [App::LinkElement] Link011_i0
  LinkedObject = -> Link010
  _LinkOwner = 4838
FEATURE [App::LinkElement] Link011_i1
  LinkPlacement = pos=(0,0,0) rot=(0,0,1;0.785398rad)
  LinkedObject = -> Link010
  Placement = pos=(0,0,0) rot=(0,0,1;0.785398rad)
  _LinkOwner = 4838
FEATURE [App::LinkElement] Link011_i2
  LinkPlacement = pos=(0,0,0) rot=(0,0,1;1.5708rad)
  LinkedObject = -> Link010
  Placement = pos=(0,0,0) rot=(0,0,1;1.5708rad)
  _LinkOwner = 4838
FEATURE [App::LinkElement] Link011_i3
  LinkPlacement = pos=(0,0,0) rot=(0,0,1;3.14159rad)
  LinkedObject = -> Link010
  Placement = pos=(0,0,0) rot=(0,0,1;3.14159rad)
  _LinkOwner = 4838
FEATURE [App::LinkElement] Link011_i4
  LinkPlacement = pos=(0,0,0) rot=(0,0,1;3.92699rad)
  LinkedObject = -> Link010
  Placement = pos=(0,0,0) rot=(0,0,1;3.92699rad)
  _LinkOwner = 4838
FEATURE [App::LinkElement] Link011_i5
  LinkPlacement = pos=(0,0,0) rot=(0,0,1;4.71239rad)
  LinkedObject = -> Link010
  Placement = pos=(0,0,0) rot=(0,0,1;4.71239rad)
  _LinkOwner = 4838
FEATURE [App::Link] Link011  label="all brackets"
  ElementCount = 6
  ElementList = -> [Link011_i0,Link011_i1,Link011_i2,Link011_i3,Link011_i4,Link011_i5]
  LinkedObject = -> Link010
FEATURE [App::Part] Part017  label="mid plate bracket fasteners"
  Group = -> [Part018,Link010,Link011]
  Origin = -> Origin031
FEATURE [Part::FeaturePython] Washer040  label="M4-Washer"  # WARN: FeaturePython — macro-defined, semantics opaque (R4)
  BaseObject = -> upper_panel [Chamfer.Edge26]
  Diameter = 5
  Invert = false
  MatchOuter = true
  OffsetAngle = 0
  Placement = pos=(-75,-212.5,371) rot=(1,0,0;1.5708rad)
  Type = 8
FEATURE [Part::FeaturePython] Screw024  label="M4x10-Screw"  # WARN: FeaturePython — macro-defined, semantics opaque (R4)
  BaseObject = -> Washer040 [Edge1]
  Diameter = 5
  Invert = false
  LeftHanded = false
  Length = 2
  LengthCustom = 10
  MatchOuter = true
  OffsetAngle = 0
  Placement = pos=(-75,-213.3,371) rot=(1,0,0;1.5708rad)
  Thread = false
  Type = 75
FEATURE [Part::FeaturePython] Washer041  label="M4-Washer"  # WARN: FeaturePython — macro-defined, semantics opaque (R4)
  BaseObject = -> upper_panel [Chamfer.Edge13]
  Diameter = 5
  Invert = false
  MatchOuter = true
  Offset = 1.5
  OffsetAngle = 0
  Placement = pos=(-75,-209.5,371) rot=(-1,0,0;1.5708rad)
  Type = 8
FEATURE [Part::FeaturePython] Nut015  label="M4-Nut"  # WARN: FeaturePython — macro-defined, semantics opaque (R4)
  BaseObject = -> Washer041 [Edge1]
  Diameter = 6
  Invert = false
  LeftHanded = false
  MatchOuter = true
  OffsetAngle = 0
  Placement = pos=(-75,-208.7,371) rot=(-1,0,0;1.5708rad)
  Thread = false
  Type = 31
FEATURE [App::Part] Part020  label="single fastener"
  Group = -> [Nut015,Washer041,Screw024,Washer040]
  Origin = -> Origin034
FEATURE [App::LinkElement] Link012_i0
  LinkedObject = -> Part020
  _LinkOwner = 4865
FEATURE [App::LinkElement] Link012_i1
  LinkPlacement = pos=(150,0,0) rot=(0,0,1;0rad)
  LinkedObject = -> Part020
  Placement = pos=(150,0,0) rot=(0,0,1;0rad)
  _LinkOwner = 4865
FEATURE [App::Link] Link012  label="single bracket"
  ElementCount = 2
  ElementList = -> [Link012_i0,Link012_i1]
  LinkedObject = -> Part020
FEATURE [App::LinkElement] Link013_i0
  LinkedObject = -> Link012
  _LinkOwner = 4868
FEATURE [App::LinkElement] Link013_i1
  LinkPlacement = pos=(0,0,0) rot=(0,0,1;0.785398rad)
  LinkedObject = -> Link012
  Placement = pos=(0,0,0) rot=(0,0,1;0.785398rad)
  _LinkOwner = 4868
FEATURE [App::LinkElement] Link013_i2
  LinkPlacement = pos=(0,0,0) rot=(0,0,1;1.5708rad)
  LinkedObject = -> Link012
  Placement = pos=(0,0,0) rot=(0,0,1;1.5708rad)
  _LinkOwner = 4868
FEATURE [App::LinkElement] Link013_i3
  LinkPlacement = pos=(0,0,0) rot=(0,0,1;2.35619rad)
  LinkedObject = -> Link012
  Placement = pos=(0,0,0) rot=(0,0,1;2.35619rad)
  _LinkOwner = 4868
FEATURE [App::LinkElement] Link013_i4
  LinkPlacement = pos=(0,0,0) rot=(0,0,1;3.14159rad)
  LinkedObject = -> Link012
  Placement = pos=(0,0,0) rot=(0,0,1;3.14159rad)
  _LinkOwner = 4868
FEATURE [App::LinkElement] Link013_i5
  LinkPlacement = pos=(0,0,0) rot=(0,0,1;3.92699rad)
  LinkedObject = -> Link012
  Placement = pos=(0,0,0) rot=(0,0,1;3.92699rad)
  _LinkOwner = 4868
FEATURE [App::LinkElement] Link013_i6
  LinkPlacement = pos=(0,0,0) rot=(0,0,1;4.71239rad)
  LinkedObject = -> Link012
  Placement = pos=(0,0,0) rot=(0,0,1;4.71239rad)
  _LinkOwner = 4868
FEATURE [App::LinkElement] Link013_i7
  LinkPlacement = pos=(0,0,0) rot=(0,0,1;5.49779rad)
  LinkedObject = -> Link012
  Placement = pos=(0,0,0) rot=(0,0,1;5.49779rad)
  _LinkOwner = 4868
FEATURE [App::LinkElement] Link013_i8
  LinkPlacement = pos=(0,0,-221) rot=(0,0,1;0.785398rad)
  LinkedObject = -> Link012
  Placement = pos=(0,0,-221) rot=(0,0,1;0.785398rad)
  _LinkOwner = 4868
FEATURE [App::LinkElement] Link013_i9
  LinkPlacement = pos=(0,0,-221) rot=(0,0,1;1.5708rad)
  LinkedObject = -> Link012
  Placement = pos=(0,0,-221) rot=(0,0,1;1.5708rad)
  _LinkOwner = 4868
FEATURE [App::LinkElement] Link013_i10
  LinkPlacement = pos=(0,0,-221) rot=(0,0,1;2.35619rad)
  LinkedObject = -> Link012
  Placement = pos=(0,0,-221) rot=(0,0,1;2.35619rad)
  _LinkOwner = 4868
FEATURE [App::LinkElement] Link013_i11
  LinkPlacement = pos=(0,0,-221) rot=(0,0,1;3.92699rad)
  LinkedObject = -> Link012
  Placement = pos=(0,0,-221) rot=(0,0,1;3.92699rad)
  _LinkOwner = 4868
FEATURE [App::LinkElement] Link013_i12
  LinkPlacement = pos=(0,0,-221) rot=(0,0,1;4.71239rad)
  LinkedObject = -> Link012
  Placement = pos=(0,0,-221) rot=(0,0,1;4.71239rad)
  _LinkOwner = 4868
FEATURE [App::LinkElement] Link013_i13
  LinkPlacement = pos=(0,0,-221) rot=(0,0,1;5.49779rad)
  LinkedObject = -> Link012
  Placement = pos=(0,0,-221) rot=(0,0,1;5.49779rad)
  _LinkOwner = 4868
FEATURE [App::Link] Link013  label="all brackets"
  ElementCount = 14
  ElementList = -> [Link013_i0,Link013_i1,Link013_i2,Link013_i3,Link013_i4,Link013_i5,Link013_i6,Link013_i7,Link013_i8,Link013_i9,Link013_i10,Link013_i11,Link013_i12,Link013_i13]
  LinkedObject = -> Link012
FEATURE [App::Part] Part019  label="upper panel bracket fasteners"
  Group = -> [Part020,Link012,Link013]
  Origin = -> Origin033
FEATURE [App::LinkElement] Link014_i0
  LinkedObject = -> Part022
  _LinkOwner = 4903
FEATURE [App::LinkElement] Link014_i1
  LinkPlacement = pos=(60,0,0) rot=(0,0,1;0rad)
  LinkedObject = -> Part022
  Placement = pos=(60,0,0) rot=(0,0,1;0rad)
  _LinkOwner = 4903
FEATURE [App::Link] Link014  label="single brace"
  ElementCount = 2
  ElementList = -> [Link014_i0,Link014_i1]
  LinkedObject = -> Part022
FEATURE [App::LinkElement] Link015_i0
  LinkedObject = -> Link014
  _LinkOwner = 4910
FEATURE [App::LinkElement] Link015_i1
  LinkPlacement = pos=(0,0,0) rot=(0,0,1;0.785398rad)
  LinkedObject = -> Link014
  Placement = pos=(0,0,0) rot=(0,0,1;0.785398rad)
  _LinkOwner = 4910
FEATURE [App::LinkElement] Link015_i2
  LinkPlacement = pos=(0,0,0) rot=(0,0,1;1.5708rad)
  LinkedObject = -> Link014
  Placement = pos=(0,0,0) rot=(0,0,1;1.5708rad)
  _LinkOwner = 4910
FEATURE [App::LinkElement] Link015_i3
  LinkPlacement = pos=(0,0,0) rot=(0,0,1;2.35619rad)
  LinkedObject = -> Link014
  Placement = pos=(0,0,0) rot=(0,0,1;2.35619rad)
  _LinkOwner = 4910
FEATURE [App::LinkElement] Link015_i4
  LinkPlacement = pos=(0,0,0) rot=(0,0,1;3.14159rad)
  LinkedObject = -> Link014
  Placement = pos=(0,0,0) rot=(0,0,1;3.14159rad)
  _LinkOwner = 4910
FEATURE [App::LinkElement] Link015_i5
  LinkPlacement = pos=(0,0,0) rot=(0,0,1;3.92699rad)
  LinkedObject = -> Link014
  Placement = pos=(0,0,0) rot=(0,0,1;3.92699rad)
  _LinkOwner = 4910
FEATURE [App::LinkElement] Link015_i6
  LinkPlacement = pos=(0,0,0) rot=(0,0,1;4.71239rad)
  LinkedObject = -> Link014
  Placement = pos=(0,0,0) rot=(0,0,1;4.71239rad)
  _LinkOwner = 4910
FEATURE [App::LinkElement] Link015_i7
  LinkPlacement = pos=(0,0,0) rot=(0,0,1;5.49779rad)
  LinkedObject = -> Link014
  Placement = pos=(0,0,0) rot=(0,0,1;5.49779rad)
  _LinkOwner = 4910
FEATURE [App::Link] Link015  label="all braces"
  ElementCount = 8
  ElementList = -> [Link015_i0,Link015_i1,Link015_i2,Link015_i3,Link015_i4,Link015_i5,Link015_i6,Link015_i7]
  LinkedObject = -> Link014
FEATURE [Part::FeaturePython] Washer044  label="M4-Washer"  # WARN: FeaturePython — macro-defined, semantics opaque (R4)
  BaseObject = -> panel009 [PolarPattern.Edge162]
  Diameter = 5
  Invert = false
  MatchOuter = true
  OffsetAngle = 0
  Placement = pos=(-30,-202,384) rot=(0,0,1;0rad)
  Type = 8
FEATURE [Part::FeaturePython] Screw026  label="M4x12-Screw"  # WARN: FeaturePython — macro-defined, semantics opaque (R4)
  BaseObject = -> Washer044 [Edge1]
  Diameter = 5
  Invert = false
  LeftHanded = false
  Length = 3
  LengthCustom = 12
  MatchOuter = true
  OffsetAngle = 0
  Placement = pos=(-30,-202,384.8) rot=(0,0,1;0rad)
  Thread = false
  Type = 75
FEATURE [Part::FeaturePython] Washer045  label="M4-Washer"  # WARN: FeaturePython — macro-defined, semantics opaque (R4)
  BaseObject = -> chamber_lid_bracket [Pocket.Edge33]
  Diameter = 5
  Invert = false
  MatchOuter = true
  OffsetAngle = 0
  Placement = pos=(-30,-202,379.5) rot=(0.317984,0.948096,0;3.14159rad)
  Type = 8
FEATURE [Part::FeaturePython] Nut017  label="M4-Nut"  # WARN: FeaturePython — macro-defined, semantics opaque (R4)
  BaseObject = -> Washer045 [Edge1]
  Diameter = 6
  Invert = false
  LeftHanded = false
  MatchOuter = true
  OffsetAngle = 0
  Placement = pos=(-30,-202,378.7) rot=(-1,0,0;3.14159rad)
  Thread = false
  Type = 31
FEATURE [App::Part] Part024  label="single fastener"
  Group = -> [Washer045,Nut017,Screw026,Washer044]
  Origin = -> Origin038
FEATURE [App::LinkElement] Link016_i0
  LinkedObject = -> Part024
  _LinkOwner = 4939
FEATURE [App::LinkElement] Link016_i1
  LinkPlacement = pos=(60,0,0) rot=(0,0,1;0rad)
  LinkedObject = -> Part024
  Placement = pos=(60,0,0) rot=(0,0,1;0rad)
  _LinkOwner = 4939
FEATURE [App::Link] Link016  label="single bracket"
  ElementCount = 2
  ElementList = -> [Link016_i0,Link016_i1]
  LinkedObject = -> Part024
FEATURE [App::LinkElement] Link017_i0
  LinkedObject = -> Link016
  _LinkOwner = 4942
FEATURE [App::LinkElement] Link017_i1
  LinkPlacement = pos=(0,0,0) rot=(0,0,1;0.785398rad)
  LinkedObject = -> Link016
  Placement = pos=(0,0,0) rot=(0,0,1;0.785398rad)
  _LinkOwner = 4942
FEATURE [App::LinkElement] Link017_i2
  LinkPlacement = pos=(0,0,0) rot=(0,0,1;1.5708rad)
  LinkedObject = -> Link016
  Placement = pos=(0,0,0) rot=(0,0,1;1.5708rad)
  _LinkOwner = 4942
FEATURE [App::LinkElement] Link017_i3
  LinkPlacement = pos=(0,0,0) rot=(0,0,1;2.35619rad)
  LinkedObject = -> Link016
  Placement = pos=(0,0,0) rot=(0,0,1;2.35619rad)
  _LinkOwner = 4942
FEATURE [App::LinkElement] Link017_i4
  LinkPlacement = pos=(0,0,0) rot=(0,0,1;3.14159rad)
  LinkedObject = -> Link016
  Placement = pos=(0,0,0) rot=(0,0,1;3.14159rad)
  _LinkOwner = 4942
FEATURE [App::LinkElement] Link017_i5
  LinkPlacement = pos=(0,0,0) rot=(0,0,1;3.92699rad)
  LinkedObject = -> Link016
  Placement = pos=(0,0,0) rot=(0,0,1;3.92699rad)
  _LinkOwner = 4942
FEATURE [App::LinkElement] Link017_i6
  LinkPlacement = pos=(0,0,0) rot=(0,0,1;4.71239rad)
  LinkedObject = -> Link016
  Placement = pos=(0,0,0) rot=(0,0,1;4.71239rad)
  _LinkOwner = 4942
FEATURE [App::LinkElement] Link017_i7
  LinkPlacement = pos=(0,0,0) rot=(0,0,1;5.49779rad)
  LinkedObject = -> Link016
  Placement = pos=(0,0,0) rot=(0,0,1;5.49779rad)
  _LinkOwner = 4942
FEATURE [App::Link] Link017  label="all brackets"
  ElementCount = 8
  ElementList = -> [Link017_i0,Link017_i1,Link017_i2,Link017_i3,Link017_i4,Link017_i5,Link017_i6,Link017_i7]
  LinkedObject = -> Link016
FEATURE [App::Part] Part023  label="top plate fasteners"
  Group = -> [Part024,Link016,Link017]
  Origin = -> Origin037
FEATURE [Part::FeaturePython] Washer046  label="M5-Washer"  # WARN: FeaturePython — macro-defined, semantics opaque (R4)
  Diameter = 6
  Invert = true
  MatchOuter = true
  OffsetAngle = 0
  Placement = pos=(215.7,-41.3,296.5) rot=(0,1,0;1.5708rad)
  Type = 8
FEATURE [Part::FeaturePython] Screw027  label="M5x14-Screw"  # WARN: FeaturePython — macro-defined, semantics opaque (R4)
  BaseObject = -> Washer046 [Edge1]
  Diameter = 6
  Invert = false
  LeftHanded = false
  Length = 3
  LengthCustom = 14
  MatchOuter = true
  OffsetAngle = 0
  Placement = pos=(216.7,-41.3,296.5) rot=(0,1,0;1.5708rad)
  Thread = false
  Type = 75
FEATURE [Part::FeaturePython] Washer047  label="M5-Washer"  # WARN: FeaturePython — macro-defined, semantics opaque (R4)
  BaseObject = -> _37DSS001 [Edge15]
  Diameter = 6
  Invert = true
  MatchOuter = true
  OffsetAngle = 0
  Placement = pos=(209.8,-41.3,296.5) rot=(0,-1,0;1.5708rad)
  Type = 8
FEATURE [Part::FeaturePython] Nut018  label="M5-Nut"  # WARN: FeaturePython — macro-defined, semantics opaque (R4)
  BaseObject = -> Washer047 [Edge1]
  Diameter = 7
  Invert = false
  LeftHanded = false
  MatchOuter = true
  OffsetAngle = 0
  Placement = pos=(208.8,-41.3,296.5) rot=(0,-1,0;1.5708rad)
  Thread = false
  Type = 31
FEATURE [App::Part] Part026  label="single fastener"
  Group = -> [Screw027,Washer046,Washer047,Nut018]
  Origin = -> Origin040
FEATURE [App::LinkElement] Link018_i0
  LinkedObject = -> Part026
  _LinkOwner = 4972
FEATURE [App::LinkElement] Link018_i1
  LinkPlacement = pos=(0,82.6,0) rot=(0,0,1;0rad)
  LinkedObject = -> Part026
  Placement = pos=(0,82.6,0) rot=(0,0,1;0rad)
  _LinkOwner = 4972
FEATURE [App::LinkElement] Link018_i2
  LinkPlacement = pos=(0,12.75,-36.5) rot=(0,0,1;0rad)
  LinkedObject = -> Part026
  Placement = pos=(0,12.75,-36.5) rot=(0,0,1;0rad)
  _LinkOwner = 4972
FEATURE [App::LinkElement] Link018_i3
  LinkPlacement = pos=(0,69.85,-36.5) rot=(0,0,1;0rad)
  LinkedObject = -> Part026
  Placement = pos=(0,69.85,-36.5) rot=(0,0,1;0rad)
  _LinkOwner = 4972
FEATURE [App::Link] Link018  label="single handle"
  ElementCount = 4
  ElementList = -> [Link018_i0,Link018_i1,Link018_i2,Link018_i3]
  LinkedObject = -> Part026
FEATURE [App::LinkElement] Link019_i0
  LinkedObject = -> Link018
  _LinkOwner = 4977
FEATURE [App::LinkElement] Link019_i1
  LinkPlacement = pos=(0,0,0) rot=(0,0,1;3.14159rad)
  LinkedObject = -> Link018
  Placement = pos=(0,0,0) rot=(0,0,1;3.14159rad)
  _LinkOwner = 4977
FEATURE [App::Link] Link019  label="both handles"
  ElementCount = 2
  ElementList = -> [Link019_i0,Link019_i1]
  LinkedObject = -> Link018
FEATURE [App::Part] Part025  label="lifting handle fasteners"
  Group = -> [Part026,Link018,Link019]
  Origin = -> Origin039
FEATURE [Part::FeaturePython] Washer  label="M8-Washer"  # WARN: FeaturePython — macro-defined, semantics opaque (R4)
  BaseObject = -> Body [Hole001.Edge41]
  Diameter = 8
  Invert = false
  MatchOuter = false
  OffsetAngle = 0
  Placement = pos=(-125,-125,-3) rot=(-1,0,0;3.14159rad)
  Type = 8
FEATURE [Part::FeaturePython] Washer048  label="M8-Washer"  # WARN: FeaturePython — macro-defined, semantics opaque (R4)
  BaseObject = -> Body [Hole001.Edge16]
  Diameter = 8
  Invert = false
  MatchOuter = false
  OffsetAngle = 0
  Placement = pos=(-125,-125,0) rot=(0,0,1;0rad)
  Type = 8
FEATURE [Part::FeaturePython] Nut  label="M8-Nut"  # WARN: FeaturePython — macro-defined, semantics opaque (R4)
  BaseObject = -> Washer048 [Edge1]
  Diameter = 9
  Invert = false
  LeftHanded = false
  MatchOuter = false
  OffsetAngle = 0
  Placement = pos=(-125,-125,1.6) rot=(0,0,1;0rad)
  Thread = false
  Type = 31
FEATURE [App::Part] Part027  label="single foot"
  Group = -> [Nut,Washer048,Washer]
  Origin = -> Origin042
FEATURE [App::LinkElement] Link020_i0
  LinkedObject = -> Part027
  _LinkOwner = 5007
FEATURE [App::LinkElement] Link020_i1
  LinkPlacement = pos=(250,0,0) rot=(0,0,1;0rad)
  LinkedObject = -> Part027
  Placement = pos=(250,0,0) rot=(0,0,1;0rad)
  _LinkOwner = 5007
FEATURE [App::LinkElement] Link020_i2
  LinkPlacement = pos=(0,250,0) rot=(0,0,1;0rad)
  LinkedObject = -> Part027
  Placement = pos=(0,250,0) rot=(0,0,1;0rad)
  _LinkOwner = 5007
FEATURE [App::LinkElement] Link020_i3
  LinkPlacement = pos=(250,250,0) rot=(0,0,1;0rad)
  LinkedObject = -> Part027
  Placement = pos=(250,250,0) rot=(0,0,1;0rad)
  _LinkOwner = 5007
FEATURE [App::Link] Link020  label="all feet"
  ElementCount = 4
  ElementList = -> [Link020_i0,Link020_i1,Link020_i2,Link020_i3]
  LinkedObject = -> Part027
FEATURE [App::Part] Part  label="foot fasteners"
  Group = -> [Part027,Link020]
  Origin = -> Origin041
FEATURE [App::Link] foot_fasteners  label="foot fasteners"
  LinkedObject = -> Part
FEATURE [App::FeaturePython] Joint241  label="foot fasteners"  # Assembly joint (typed FeaturePython)
  Activated = true
  AngleMax = 0
  AngleMin = 0
  Detach1 = false
  Detach2 = false
  Distance = 0
  Distance2 = 0
  EnableAngleMax = false
  EnableAngleMin = false
  EnableLengthMax = false
  EnableLengthMin = false
  JointType = 0 (Fixed)
  LengthMax = 0
  LengthMin = 0
  Placement2 = pos=(-125,-125,-3) rot=(1,0,0;3.14159rad)
  Reference1 = -> Assembly [foot_fasteners.Link020.Link020_i0.Washer.Edge3,foot_fasteners.Link020.Link020_i0.Washer.Edge3]
  Reference2 = -> Assembly [Body.Edge41,Body.Edge41]
FEATURE [App::Link] lower_panel_block_fasteners  label="lower panel block fasteners"
  LinkPlacement = pos=(-1.95e-14,6.39e-14,8.79e-14) rot=(0,0,1;0rad)
  LinkedObject = -> Part005
  Placement = pos=(-1.95e-14,6.39e-14,8.79e-14) rot=(0,0,1;0rad)
FEATURE [App::FeaturePython] Joint246  label="lower panel block fasteners"  # Assembly joint (typed FeaturePython)
  Activated = true
  AngleMax = 0
  AngleMin = 0
  Detach1 = false
  Detach2 = false
  Distance = 0
  Distance2 = 0
  EnableAngleMax = false
  EnableAngleMin = false
  EnableLengthMax = false
  EnableLengthMin = false
  JointType = 0 (Fixed)
  LengthMax = 0
  LengthMin = 0
  Placement2 = pos=(-75,2.84e-14,-60) rot=(1,0,0;1.5708rad)
  Reference1 = -> Assembly [lower_panel_block_fasteners.Link005.Link005_i0.Link004_i0.Washer029.Edge3,lower_panel_block_fasteners.Link005.Link005_i0.Link004_i0.Washer029.Edge3]
  Reference2 = -> Assembly [OCT_LFPNL_BA.Edge12,OCT_LFPNL_BA.Edge12]
FEATURE [App::Link] lower_panel_bracket_fasteners  label="lower panel bracket fasteners"
  LinkPlacement = pos=(2.39e-14,8.36e-14,6.46e-14) rot=(0,0,1;0rad)
  LinkedObject = -> Part004
  Placement = pos=(2.39e-14,8.36e-14,6.46e-14) rot=(0,0,1;0rad)
FEATURE [App::FeaturePython] Joint247  label="lower panel bracket fasteners"  # Assembly joint (typed FeaturePython)
  Activated = true
  AngleMax = 0
  AngleMin = 0
  Detach1 = false
  Detach2 = false
  Distance = 0
  Distance2 = 0
  EnableAngleMax = false
  EnableAngleMin = false
  EnableLengthMax = false
  EnableLengthMin = false
  JointType = 0 (Fixed)
  LengthMax = 0
  LengthMin = 0
  Offset2 = pos=(0,0,0) rot=(0,0,-1;0.785398rad)
  Placement2 = pos=(-75,-2.84e-14,-60) rot=(0.862856,0.357407,-0.357407;1.71777rad)
  Reference1 = -> Assembly [lower_panel_bracket_fasteners.Link007.Link007_i0.Link006_i0.Washer027.Edge3,lower_panel_bracket_fasteners.Link007.Link007_i0.Link006_i0.Washer027.Edge3]
  Reference2 = -> Assembly [OCT_LFPNL_AB.Edge12,OCT_LFPNL_AB.Edge12]
FEATURE [App::Link] baseplate_block_fasteners  label="baseplate block fasteners"
  LinkedObject = -> Part007
FEATURE [App::FeaturePython] Joint248  label="baseplate block fasteners"  # Assembly joint (typed FeaturePython)
  Activated = true
  AngleMax = 0
  AngleMin = 0
  Detach1 = false
  Detach2 = false
  Distance = 0
  Distance2 = 0
  EnableAngleMax = false
  EnableAngleMin = false
  EnableLengthMax = false
  EnableLengthMin = false
  JointType = 0 (Fixed)
  LengthMax = 0
  LengthMin = 0
  Placement2 = pos=(-70,-201,-3) rot=(1,0,0;3.14159rad)
  Reference1 = -> Assembly [baseplate_block_fasteners.Link003.Link003_i0.Link002_i0.Washer032.Edge3,baseplate_block_fasteners.Link003.Link003_i0.Link002_i0.Washer032.Edge3]
  Reference2 = -> Assembly [Body.Edge43,Body.Edge43]
FEATURE [App::Link] baseplate_bracket_fasteners  label="baseplate bracket fasteners"
  LinkPlacement = pos=(-3.2e-15,-7.3e-15,1.98e-14) rot=(0,0,1;0rad)
  LinkedObject = -> Part009
  Placement = pos=(-3.2e-15,-7.3e-15,1.98e-14) rot=(0,0,1;0rad)
FEATURE [App::FeaturePython] Joint249  label="baseplate bracket fasteners"  # Assembly joint (typed FeaturePython)
  Activated = true
  AngleMax = 0
  AngleMin = 0
  Detach1 = false
  Detach2 = false
  Distance = 0
  Distance2 = 0
  EnableAngleMax = false
  EnableAngleMin = false
  EnableLengthMax = false
  EnableLengthMin = false
  JointType = 0 (Fixed)
  LengthMax = 0
  LengthMin = 0
  Offset2 = pos=(0,0,0) rot=(0,0,1;0.785398rad)
  Placement2 = pos=(92.631,-191.626,-3) rot=(1,0,0;3.14159rad)
  Reference1 = -> Assembly [baseplate_bracket_fasteners.Link001.Link001_i0.Link_i0.Washer034.Edge3,baseplate_bracket_fasteners.Link001.Link001_i0.Link_i0.Washer034.Edge3]
  Reference2 = -> Assembly [Body.Edge47,Body.Edge47]
FEATURE [App::Link] mid_plate_block_fasteners  label="mid plate block fasteners"
  LinkPlacement = pos=(-3.2e-15,-9.05e-14,1.07e-14) rot=(0,0,1;0rad)
  LinkedObject = -> Part015
  Placement = pos=(-3.2e-15,-9.05e-14,1.07e-14) rot=(0,0,1;0rad)
FEATURE [App::Link] mid_plate_bracket_fasteners  label="mid plate bracket fasteners"
  LinkPlacement = pos=(-2.06e-14,-8.25e-14,1.7e-15) rot=(0,0,1;0rad)
  LinkedObject = -> Part017
  Placement = pos=(-2.06e-14,-8.25e-14,1.7e-15) rot=(0,0,1;0rad)
FEATURE [App::Link] upper_panel_block_fasteners  label="upper panel block fasteners"
  LinkPlacement = pos=(-4.03e-14,-2.4e-15,-3.1e-14) rot=(0,0,1;0rad)
  LinkedObject = -> Part013
  Placement = pos=(-4.03e-14,-2.4e-15,-3.1e-14) rot=(0,0,1;0rad)
FEATURE [App::FeaturePython] Joint252  label="upper panel block fasteners"  # Assembly joint (typed FeaturePython)
  Activated = true
  AngleMax = 0
  AngleMin = 0
  Detach1 = false
  Detach2 = false
  Distance = 0
  Distance2 = 0
  EnableAngleMax = false
  EnableAngleMin = false
  EnableLengthMax = false
  EnableLengthMin = false
  JointType = 0 (Fixed)
  LengthMax = 0
  LengthMin = 0
  Placement2 = pos=(-75,-1.5,10) rot=(1,0,0;1.5708rad)
  Reference1 = -> Assembly [upper_panel_block_fasteners.Link008.Link008_i0.Washer036.Edge3,upper_panel_block_fasteners.Link008.Link008_i0.Washer036.Edge3]
  Reference2 = -> Assembly [upper_panel.Edge25,upper_panel.Edge25]
FEATURE [App::Link] upper_panel_bracket_fasteners  label="upper panel bracket fasteners"
  LinkPlacement = pos=(-4.37e-14,3.15e-14,-9.25e-14) rot=(0,0,1;0rad)
  LinkedObject = -> Part019
  Placement = pos=(-4.37e-14,3.15e-14,-9.25e-14) rot=(0,0,1;0rad)
FEATURE [App::FeaturePython] Joint253  label="upper panel bracket fasteners"  # Assembly joint (typed FeaturePython)
  Activated = true
  AngleMax = 0
  AngleMin = 0
  Detach1 = false
  Detach2 = false
  Distance = 0
  Distance2 = 0
  EnableAngleMax = false
  EnableAngleMin = false
  EnableLengthMax = false
  EnableLengthMin = false
  JointType = 0 (Fixed)
  LengthMax = 0
  LengthMin = 0
  Placement2 = pos=(-75,-1.5,231) rot=(1,0,0;1.5708rad)
  Reference1 = -> Assembly [upper_panel_bracket_fasteners.Link013.Link013_i0.Link012_i0.Washer040.Edge3,upper_panel_bracket_fasteners.Link013.Link013_i0.Link012_i0.Washer040.Edge3]
  Reference2 = -> Assembly [upper_panel.Edge26,upper_panel.Edge26]
FEATURE [App::Link] top_plate_fasteners  label="top plate fasteners"
  LinkPlacement = pos=(-1.41e-14,-2.758e-13,-1.53e-13) rot=(0,0,1;0rad)
  LinkedObject = -> Part023
  Placement = pos=(-1.41e-14,-2.758e-13,-1.53e-13) rot=(0,0,1;0rad)
FEATURE [App::FeaturePython] Joint255  label="top plate fasteners"  # Assembly joint (typed FeaturePython)
  Activated = true
  AngleMax = 0
  AngleMin = 0
  Detach1 = false
  Detach2 = false
  Distance = 0
  Distance2 = 0
  EnableAngleMax = false
  EnableAngleMin = false
  EnableLengthMax = false
  EnableLengthMin = false
  JointType = 0 (Fixed)
  LengthMax = 0
  LengthMin = 0
  Offset2 = pos=(0,0,0) rot=(0,0,1;3.14159rad)
  Placement2 = pos=(30,-202,-3) rot=(0,1,0;3.14159rad)
  Reference1 = -> Assembly [top_plate_fasteners.Link017.Link017_i0.Link016_i0.Washer044.Edge3,top_plate_fasteners.Link017.Link017_i0.Link016_i0.Washer044.Edge3]
  Reference2 = -> Assembly [panel009.Edge162,panel009.Edge162]
FEATURE [App::Link] lifting_handle_fasteners  label="lifting handle fasteners"
  LinkPlacement = pos=(-7.17e-14,-5.4e-14,6.01e-14) rot=(0,0,1;0rad)
  LinkedObject = -> Part025
  Placement = pos=(-7.17e-14,-5.4e-14,6.01e-14) rot=(0,0,1;0rad)
FEATURE [App::FeaturePython] Joint188  label="chamber brace 2"  # Assembly joint (typed FeaturePython)
  Activated = true
  AngleMax = 0
  AngleMin = 0
  Detach1 = false
  Detach2 = false
  Distance = 0
  Distance2 = 0
  EnableAngleMax = false
  EnableAngleMin = false
  EnableLengthMax = false
  EnableLengthMin = false
  JointType = 0 (Fixed)
  LengthMax = 0
  LengthMin = 0
  Offset1 = pos=(0,-2.5,0) rot=(0,0,1;0rad)
  Offset2 = pos=(0,0,0) rot=(0,0,-1;1.5708rad)
  Placement1 = pos=(67.8823,-110.309,0) rot=(0,0,1;3.92699rad)
  Placement2 = pos=(-30,-15,0) rot=(0,1,0;3.14159rad)
  Reference1 = -> Assembly [Body017.Edge36,Body017.Edge36]
  Reference2 = -> Assembly [brace001.Edge25,brace001.Edge25]
FEATURE [App::FeaturePython] Joint125  label="ub base 2"  # Assembly joint (typed FeaturePython)
  Activated = true
  AngleMax = 0
  AngleMin = 0
  Detach1 = false
  Detach2 = false
  Distance = 0
  Distance2 = 0
  EnableAngleMax = false
  EnableAngleMin = false
  EnableLengthMax = false
  EnableLengthMin = false
  JointType = 0 (Fixed)
  LengthMax = 0
  LengthMin = 0
  Offset2 = pos=(0,0,0) rot=(0,0,-1;1.5708rad)
  Placement1 = pos=(-70,10,5.68e-14) rot=(0,0,1;1.5708rad)
  Placement2 = pos=(92.631,-191.626,-3) rot=(0.382683,0.92388,0;3.14159rad)
  Reference1 = -> Assembly [bracket009.Edge24,bracket009.Edge24]
  Reference2 = -> Assembly [Body017.Edge162,Body017.Edge162]
FEATURE [App::FeaturePython] Joint126  label="ub base 3"  # Assembly joint (typed FeaturePython)
  Activated = true
  AngleMax = 0
  AngleMin = 0
  Detach1 = false
  Detach2 = false
  Distance = 0
  Distance2 = 0
  EnableAngleMax = false
  EnableAngleMin = false
  EnableLengthMax = false
  EnableLengthMin = false
  JointType = 0 (Fixed)
  LengthMax = 0
  LengthMin = 0
  Offset2 = pos=(0,0,0) rot=(0,0,-1;1.5708rad)
  Placement1 = pos=(-70,10,0) rot=(0,0,1;1.5708rad)
  Placement2 = pos=(201,-70,-3) rot=(0,1,0;3.14159rad)
  Reference1 = -> Assembly [bracket010.Edge24,bracket010.Edge24]
  Reference2 = -> Assembly [Body017.Edge206,Body017.Edge206]
FEATURE [App::FeaturePython] Joint127  label="ub base 4"  # Assembly joint (typed FeaturePython)
  Activated = true
  AngleMax = 0
  AngleMin = 0
  Detach1 = false
  Detach2 = false
  Distance = 0
  Distance2 = 0
  EnableAngleMax = false
  EnableAngleMin = false
  EnableLengthMax = false
  EnableLengthMin = false
  JointType = 0 (Fixed)
  LengthMax = 0
  LengthMin = 0
  Offset2 = pos=(0,0,0) rot=(0,0,-1;1.5708rad)
  Placement1 = pos=(-70,10,2.84e-14) rot=(0,0,1;1.5708rad)
  Placement2 = pos=(191.626,92.631,-3) rot=(-0.382683,0.92388,0;3.14159rad)
  Reference1 = -> Assembly [bracket011.Edge24,bracket011.Edge24]
  Reference2 = -> Assembly [Body017.Edge278,Body017.Edge278]
FEATURE [App::FeaturePython] Joint129  label="ub base 6"  # Assembly joint (typed FeaturePython)
  Activated = true
  AngleMax = 0
  AngleMin = 0
  Detach1 = false
  Detach2 = false
  Distance = 0
  Distance2 = 0
  EnableAngleMax = false
  EnableAngleMin = false
  EnableLengthMax = false
  EnableLengthMin = false
  JointType = 0 (Fixed)
  LengthMax = 0
  LengthMin = 0
  Offset2 = pos=(0,0,0) rot=(0,0,-1;1.5708rad)
  Placement1 = pos=(-70,10,5.68e-14) rot=(0,0,-1;4.71239rad)
  Placement2 = pos=(-92.631,191.626,-3) rot=(-0.92388,0.382683,0;3.14159rad)
  Reference1 = -> Assembly [bracket013.Edge24,bracket013.Edge24]
  Reference2 = -> Assembly [Body017.Edge254,Body017.Edge254]
FEATURE [App::FeaturePython] Joint130  label="ub base 7"  # Assembly joint (typed FeaturePython)
  Activated = true
  AngleMax = 0
  AngleMin = 0
  Detach1 = false
  Detach2 = false
  Distance = 0
  Distance2 = 0
  EnableAngleMax = false
  EnableAngleMin = false
  EnableLengthMax = false
  EnableLengthMin = false
  JointType = 0 (Fixed)
  LengthMax = 0
  LengthMin = 0
  Offset2 = pos=(0,0,0) rot=(0,0,-1;1.5708rad)
  Placement1 = pos=(-70,10,5.68e-14) rot=(0,0,-1;4.71239rad)
  Placement2 = pos=(-201,70,-3) rot=(-1,0,0;3.14159rad)
  Reference1 = -> Assembly [bracket014.Edge24,bracket014.Edge24]
  Reference2 = -> Assembly [Body017.Edge226,Body017.Edge226]
FEATURE [App::FeaturePython] Joint131  label="ub base 8"  # Assembly joint (typed FeaturePython)
  Activated = true
  AngleMax = 0
  AngleMin = 0
  Detach1 = false
  Detach2 = false
  Distance = 0
  Distance2 = 0
  EnableAngleMax = false
  EnableAngleMin = false
  EnableLengthMax = false
  EnableLengthMin = false
  JointType = 0 (Fixed)
  LengthMax = 0
  LengthMin = 0
  Offset2 = pos=(0,0,0) rot=(0,0,-1;1.5708rad)
  Placement1 = pos=(-70,10,2.84e-14) rot=(0,0,1;1.5708rad)
  Placement2 = pos=(-191.626,-92.631,-3) rot=(0.92388,0.382683,0;3.14159rad)
  Reference1 = -> Assembly [bracket015.Edge24,bracket015.Edge24]
  Reference2 = -> Assembly [Body017.Edge138,Body017.Edge138]
FEATURE [App::FeaturePython] Joint175  label="chamber plate - u panel"  # Assembly joint (typed FeaturePython)
  Activated = true
  AngleMax = 0
  AngleMin = 0
  Detach1 = false
  Detach2 = false
  Distance = 0
  Distance2 = 0
  EnableAngleMax = false
  EnableAngleMin = false
  EnableLengthMax = false
  EnableLengthMin = false
  JointType = 0 (Fixed)
  LengthMax = 0
  LengthMin = 0
  Placement1 = pos=(-70,10,40) rot=(0,0,1;0rad)
  Placement2 = pos=(-70,-201,-3) rot=(1,0,0;3.14159rad)
  Reference1 = -> Assembly [upper_left_block.Edge14,upper_left_block.Edge14]
  Reference2 = -> Assembly [Body017.Edge120,Body017.Edge120]
FEATURE [App::FeaturePython] Joint177  label="chamber plate - u block FR"  # Assembly joint (typed FeaturePython)
  Activated = true
  AngleMax = 0
  AngleMin = 0
  Detach1 = false
  Detach2 = false
  Distance = 0
  Distance2 = 0
  EnableAngleMax = false
  EnableAngleMin = false
  EnableLengthMax = false
  EnableLengthMin = false
  JointType = 0 (Fixed)
  LengthMax = 0
  LengthMin = 0
  Placement1 = pos=(70,10,40) rot=(0,0,1;0rad)
  Placement2 = pos=(70,-201,-3) rot=(1,0,0;3.14159rad)
  Reference1 = -> Assembly [upper_right_block.Edge14,upper_right_block.Edge14]
  Reference2 = -> Assembly [Body017.Edge160,Body017.Edge160]
FEATURE [App::FeaturePython] Joint178  label="chamber plate - u block RL"  # Assembly joint (typed FeaturePython)
  Activated = true
  AngleMax = 0
  AngleMin = 0
  Detach1 = false
  Detach2 = false
  Distance = 0
  Distance2 = 0
  EnableAngleMax = false
  EnableAngleMin = false
  EnableLengthMax = false
  EnableLengthMin = false
  JointType = 0 (Fixed)
  LengthMax = 0
  LengthMin = 0
  Placement1 = pos=(-70,10,40) rot=(0,0,1;0rad)
  Placement2 = pos=(70,201,-3) rot=(0,1,0;3.14159rad)
  Reference1 = -> Assembly [upper_left_block001.Edge14,upper_left_block001.Edge14]
  Reference2 = -> Assembly [Body017.Edge298,Body017.Edge298]
FEATURE [App::FeaturePython] Joint179  label="chamber plate - u block RR"  # Assembly joint (typed FeaturePython)
  Activated = true
  AngleMax = 0
  AngleMin = 0
  Detach1 = false
  Detach2 = false
  Distance = 0
  Distance2 = 0
  EnableAngleMax = false
  EnableAngleMin = false
  EnableLengthMax = false
  EnableLengthMin = false
  JointType = 0 (Fixed)
  LengthMax = 0
  LengthMin = 0
  Placement1 = pos=(70,10,40) rot=(0,0,1;0rad)
  Placement2 = pos=(-70,201,-3) rot=(0,1,0;3.14159rad)
  Reference1 = -> Assembly [upper_right_block001.Edge14,upper_right_block001.Edge14]
  Reference2 = -> Assembly [Body017.Edge256,Body017.Edge256]
FEATURE [App::FeaturePython] Joint187  label="chamber brace 1"  # Assembly joint (typed FeaturePython)
  Activated = true
  AngleMax = 0
  AngleMin = 0
  Detach1 = false
  Detach2 = false
  Distance = 0
  Distance2 = 0
  EnableAngleMax = false
  EnableAngleMin = false
  EnableLengthMax = false
  EnableLengthMin = false
  JointType = 0 (Fixed)
  LengthMax = 0
  LengthMin = 0
  Offset1 = pos=(0,-2.5,0) rot=(0,0,1;0rad)
  Offset2 = pos=(0,0,0) rot=(0,0,-1;1.5708rad)
  Placement1 = pos=(-30,-126,0) rot=(0,0,1;3.14159rad)
  Placement2 = pos=(-30,-15,0) rot=(0,1,0;3.14159rad)
  Reference1 = -> Assembly [Body017.Edge15,Body017.Edge15]
  Reference2 = -> Assembly [brace.Edge25,brace.Edge25]
FEATURE [App::FeaturePython] Joint189  label="chamber brace 3"  # Assembly joint (typed FeaturePython)
  Activated = true
  AngleMax = 0
  AngleMin = 0
  Detach1 = false
  Detach2 = false
  Distance = 0
  Distance2 = 0
  EnableAngleMax = false
  EnableAngleMin = false
  EnableLengthMax = false
  EnableLengthMin = false
  JointType = 0 (Fixed)
  LengthMax = 0
  LengthMin = 0
  Offset1 = pos=(0,-2.5,0) rot=(0,0,1;0rad)
  Offset2 = pos=(0,0,0) rot=(0,0,-1;1.5708rad)
  Placement1 = pos=(126,-30,0) rot=(0,0,-1;1.5708rad)
  Placement2 = pos=(-30,-15,2.84e-14) rot=(0,1,0;3.14159rad)
  Reference1 = -> Assembly [Body017.Edge54,Body017.Edge54]
  Reference2 = -> Assembly [brace002.Edge25,brace002.Edge25]
FEATURE [App::FeaturePython] Joint190  label="chamber brace 4"  # Assembly joint (typed FeaturePython)
  Activated = true
  AngleMax = 0
  AngleMin = 0
  Detach1 = false
  Detach2 = false
  Distance = 0
  Distance2 = 0
  EnableAngleMax = false
  EnableAngleMin = false
  EnableLengthMax = false
  EnableLengthMin = false
  JointType = 0 (Fixed)
  LengthMax = 0
  LengthMin = 0
  Offset1 = pos=(0,-2.5,0) rot=(0,0,1;0rad)
  Offset2 = pos=(0,0,0) rot=(0,0,-1;1.5708rad)
  Placement1 = pos=(110.309,67.8823,0) rot=(0,0,-1;0.785398rad)
  Placement2 = pos=(-30,-15,0) rot=(0,1,0;3.14159rad)
  Reference1 = -> Assembly [Body017.Edge84,Body017.Edge84]
  Reference2 = -> Assembly [brace003.Edge25,brace003.Edge25]
FEATURE [App::FeaturePython] Joint191  label="chamber brace 5"  # Assembly joint (typed FeaturePython)
  Activated = true
  AngleMax = 0
  AngleMin = 0
  Detach1 = false
  Detach2 = false
  Distance = 0
  Distance2 = 0
  EnableAngleMax = false
  EnableAngleMin = false
  EnableLengthMax = false
  EnableLengthMin = false
  JointType = 0 (Fixed)
  LengthMax = 0
  LengthMin = 0
  Offset1 = pos=(0,-2.5,0) rot=(0,0,1;0rad)
  Offset2 = pos=(0,0,0) rot=(0,0,-1;1.5708rad)
  Placement1 = pos=(30,126,0) rot=(0,0,1;0rad)
  Placement2 = pos=(-30,-15,0) rot=(0,1,0;3.14159rad)
  Reference1 = -> Assembly [Body017.Edge90,Body017.Edge90]
  Reference2 = -> Assembly [brace004.Edge25,brace004.Edge25]
FEATURE [App::FeaturePython] Joint192  label="chamber brace 6"  # Assembly joint (typed FeaturePython)
  Activated = true
  AngleMax = 0
  AngleMin = 0
  Detach1 = false
  Detach2 = false
  Distance = 0
  Distance2 = 0
  EnableAngleMax = false
  EnableAngleMin = false
  EnableLengthMax = false
  EnableLengthMin = false
  JointType = 0 (Fixed)
  LengthMax = 0
  LengthMin = 0
  Offset1 = pos=(0,-2.5,0) rot=(0,0,1;0rad)
  Offset2 = pos=(0,0,0) rot=(0,0,-1;1.5708rad)
  Placement1 = pos=(-67.8823,110.309,0) rot=(0,0,1;0.785398rad)
  Placement2 = pos=(-30,-15,0) rot=(0,-1,0;3.14159rad)
  Reference1 = -> Assembly [Body017.Edge69,Body017.Edge69]
  Reference2 = -> Assembly [brace005.Edge25,brace005.Edge25]
FEATURE [App::FeaturePython] Joint193  label="chamber brace 7"  # Assembly joint (typed FeaturePython)
  Activated = true
  AngleMax = 0
  AngleMin = 0
  Detach1 = false
  Detach2 = false
  Distance = 0
  Distance2 = 0
  EnableAngleMax = false
  EnableAngleMin = false
  EnableLengthMax = false
  EnableLengthMin = false
  JointType = 0 (Fixed)
  LengthMax = 0
  LengthMin = 0
  Offset1 = pos=(0,-2.5,0) rot=(0,0,1;0rad)
  Offset2 = pos=(0,0,0) rot=(0,0,-1;1.5708rad)
  Placement1 = pos=(-126,30,0) rot=(0,0,1;1.5708rad)
  Placement2 = pos=(-30,-15,0) rot=(0,1,0;3.14159rad)
  Reference1 = -> Assembly [Body017.Edge59,Body017.Edge59]
  Reference2 = -> Assembly [brace006.Edge25,brace006.Edge25]
FEATURE [App::FeaturePython] Joint194  label="chamber brace 8"  # Assembly joint (typed FeaturePython)
  Activated = true
  AngleMax = 0
  AngleMin = 0
  Detach1 = false
  Detach2 = false
  Distance = 0
  Distance2 = 0
  EnableAngleMax = false
  EnableAngleMin = false
  EnableLengthMax = false
  EnableLengthMin = false
  JointType = 0 (Fixed)
  LengthMax = 0
  LengthMin = 0
  Offset1 = pos=(0,-2.5,0) rot=(0,0,1;0rad)
  Offset2 = pos=(0,0,0) rot=(0,0,-1;1.5708rad)
  Placement1 = pos=(-110.309,-67.8823,0) rot=(0,0,1;2.35619rad)
  Placement2 = pos=(-30,-15,0) rot=(0,1,0;3.14159rad)
  Reference1 = -> Assembly [Body017.Edge21,Body017.Edge21]
  Reference2 = -> Assembly [brace007.Edge25,brace007.Edge25]
FEATURE [App::FeaturePython] Joint250  label="midplate block fasteners"  # Assembly joint (typed FeaturePython)
  Activated = true
  AngleMax = 0
  AngleMin = 0
  Detach1 = false
  Detach2 = false
  Distance = 0
  Distance2 = 0
  EnableAngleMax = false
  EnableAngleMin = false
  EnableLengthMax = false
  EnableLengthMin = false
  JointType = 0 (Fixed)
  LengthMax = 0
  LengthMin = 0
  Placement2 = pos=(70,-201,0) rot=(0,0,1;0rad)
  Reference1 = -> Assembly [mid_plate_block_fasteners.Link009.Link009_i1.Washer037.Edge3,mid_plate_block_fasteners.Link009.Link009_i1.Washer037.Edge3]
  Reference2 = -> Assembly [Body017.Edge30,Body017.Edge30]
FEATURE [App::FeaturePython] Joint251  label="midplate bracket fasteners"  # Assembly joint (typed FeaturePython)
  Activated = true
  AngleMax = 0
  AngleMin = 0
  Detach1 = false
  Detach2 = false
  Distance = 0
  Distance2 = 0
  EnableAngleMax = false
  EnableAngleMin = false
  EnableLengthMax = false
  EnableLengthMin = false
  JointType = 0 (Fixed)
  LengthMax = 0
  LengthMin = 0
  Offset2 = pos=(0,0,0) rot=(0,0,-1;0.785398rad)
  Placement2 = pos=(92.631,-191.626,0) rot=(0,0,1;0rad)
  Reference1 = -> Assembly [mid_plate_bracket_fasteners.Link011.Link011_i0.Link010_i0.Washer038.Edge3,mid_plate_bracket_fasteners.Link011.Link011_i0.Link010_i0.Washer038.Edge3]
  Reference2 = -> Assembly [Body017.Edge31,Body017.Edge31]
FEATURE [Part::FeaturePython] Washer049  label="M6-Washer"  # WARN: FeaturePython — macro-defined, semantics opaque (R4)
  BaseObject = -> brace [Hole.Edge31]
  Diameter = 7
  Invert = false
  MatchOuter = false
  OffsetAngle = 0
  Placement = pos=(-30,-126,166) rot=(0,0,1;0rad)
  Type = 8
FEATURE [Part::FeaturePython] Screw  label="M6x16-Screw"  # WARN: FeaturePython — macro-defined, semantics opaque (R4)
  BaseObject = -> Washer049 [Edge1]
  Diameter = 7
  Invert = false
  LeftHanded = false
  Length = 4
  LengthCustom = 16
  MatchOuter = false
  OffsetAngle = 0
  Placement = pos=(-30,-126,167.6) rot=(0,0,1;0rad)
  Thread = false
  Type = 75
FEATURE [Part::FeaturePython] Washer050  label="M6-Washer"  # WARN: FeaturePython — macro-defined, semantics opaque (R4)
  BaseObject = -> Washer049 [Edge3]
  Diameter = 7
  Invert = true
  MatchOuter = false
  Offset = 6
  OffsetAngle = 0
  Placement = pos=(-30,-126,160) rot=(-1,0,0;3.14159rad)
  Type = 8
FEATURE [Part::FeaturePython] Nut019  label="M6-Nut"  # WARN: FeaturePython — macro-defined, semantics opaque (R4)
  BaseObject = -> Washer050 [Edge1]
  Diameter = 8
  Invert = false
  LeftHanded = false
  MatchOuter = false
  OffsetAngle = 0
  Placement = pos=(-30,-126,158.4) rot=(-1,0,0;3.14159rad)
  Thread = false
  Type = 31
FEATURE [App::Part] Part022  label="single fastener"
  Group = -> [Nut019,Washer050,Screw,Washer049]
  Origin = -> Origin036
FEATURE [App::Part] Part021  label="chamber brace fasteners"
  Group = -> [Part022,Link014,Link015]
  Origin = -> Origin035
FEATURE [App::DocumentObjectGroup] Group013  label="Fastener Groups"
  Group = -> [Part002,Part003,Part001,Part004,Part007,Part009,Part015,Part017,Part013,Part019,Part023,Part025,Part,Part005,Part021]
FEATURE [App::Link] chamber_brace_fasteners  label="chamber brace fasteners"
  LinkPlacement = pos=(-8.2e-15,-5.76e-14,-5.9e-14) rot=(0,0,1;0rad)
  LinkedObject = -> Part021
  Placement = pos=(-8.2e-15,-5.76e-14,-5.9e-14) rot=(0,0,1;0rad)
FEATURE [App::DocumentObjectGroup] Group017  label="Fasteners"
  Group = -> [lower_panel_block_fasteners,foot_fasteners,lower_panel_bracket_fasteners,baseplate_block_fasteners,baseplate_bracket_fasteners,mid_plate_block_fasteners,mid_plate_bracket_fasteners,upper_panel_block_fasteners,upper_panel_bracket_fasteners,top_plate_fasteners,lifting_handle_fasteners,chamber_brace_fasteners]
FEATURE [App::FeaturePython] Joint257  label="chamber brace fasteners"  # Assembly joint (typed FeaturePython)
  Activated = true
  AngleMax = 0
  AngleMin = 0
  Detach1 = false
  Detach2 = false
  Distance = 0
  Distance2 = 0
  EnableAngleMax = false
  EnableAngleMin = false
  EnableLengthMax = false
  EnableLengthMin = false
  JointType = 0 (Fixed)
  LengthMax = 0
  LengthMin = 0
  Offset2 = pos=(0,0,0) rot=(0,0,-1;1.5708rad)
  Placement2 = pos=(-30,-15,3) rot=(0,0,1;0rad)
  Reference1 = -> Assembly [chamber_brace_fasteners.Link015.Link015_i7.Link014_i0.Washer049.Edge3,chamber_brace_fasteners.Link015.Link015_i7.Link014_i0.Washer049.Edge3]
  Reference2 = -> Assembly [brace007.Edge31,brace007.Edge31]
FEATURE [Spreadsheet::Sheet] Fasteners_BOM
  cells = A1='Type; B1='Qty; A2='ISO4032 Nut M4; B2=92; A3='ISO4032 Nut M5; B3=8; A4='ISO4032 Nut M6; B4=24; A5='ISO4032 Nut M8; B5=4; A6='ISO4762 Screw M4x10; B6=64; A7='ISO4762 Screw M4x12; B7=48; A8='ISO4762 Screw M5x14; B8=8; A9='ISO4762 Screw M6x16; B9=26; A10='ISO7089 Washer M4; B10=204; A11='ISO7089 Washer M5; B11=16; A12='ISO7089 Washer M6; B12=50; A13='ISO7089 Washer M8; B13=8
FEATURE [App::Link] WDS673_82225  label="WDS673-82225"
  LinkPlacement = pos=(125,125,-24.9) rot=(-0.57735,0.57735,0.57735;4.18879rad)
  LinkedObject = -> <external mechanical COTS/WDS673-82225.FCStd>#WDS673_82225
  Placement = pos=(125,125,-24.9) rot=(-0.57735,0.57735,0.57735;4.18879rad)
FEATURE [App::Link] WDS673_82226  label="WDS673-82225"
  LinkPlacement = pos=(-125,125,-24.9) rot=(-0.57735,0.57735,0.57735;4.18879rad)
  LinkedObject = -> <external mechanical COTS/WDS673-82225.FCStd>#WDS673_82225
  Placement = pos=(-125,125,-24.9) rot=(-0.57735,0.57735,0.57735;4.18879rad)
FEATURE [App::Link] WDS673_82227  label="WDS673-82225"
  LinkPlacement = pos=(125,-125,-24.9) rot=(-0.57735,0.57735,0.57735;4.18879rad)
  LinkedObject = -> <external mechanical COTS/WDS673-82225.FCStd>#WDS673_82225
  Placement = pos=(125,-125,-24.9) rot=(-0.57735,0.57735,0.57735;4.18879rad)
FEATURE [App::Link] WDS673_82228  label="WDS673-82225"
  LinkPlacement = pos=(-125,-125,-24.9) rot=(-0.57735,0.57735,0.57735;4.18879rad)
  LinkedObject = -> <external mechanical COTS/WDS673-82225.FCStd>#WDS673_82225
  Placement = pos=(-125,-125,-24.9) rot=(-0.57735,0.57735,0.57735;4.18879rad)
FEATURE [App::DocumentObjectGroup] Group009  label="Feet"
  Group = -> [WDS673_82228,WDS673_82227,WDS673_82226,WDS673_82225]
FEATURE [App::FeaturePython] Joint258  label="Fixed"  # Assembly joint (typed FeaturePython)
  Activated = true
  AngleMax = 0
  AngleMin = 0
  Detach1 = false
  Detach2 = false
  Distance = 0
  Distance2 = 0
  EnableAngleMax = false
  EnableAngleMin = false
  EnableLengthMax = false
  EnableLengthMin = false
  JointType = 0 (Fixed)
  LengthMax = 0
  LengthMin = 0
  Placement1 = pos=(0,10.5,0) rot=(-0.57735,-0.57735,0.57735;4.18879rad)
  Placement2 = pos=(0,0,1.6) rot=(0,0,1;0rad)
  Reference1 = -> Assembly [WDS673_82228.Part__Feature001.Edge6,WDS673_82228.Part__Feature001.Edge6]
  Reference2 = -> Assembly [foot_fasteners.Link020.Link020_i0.Washer.Edge1,foot_fasteners.Link020.Link020_i0.Washer.Edge1]
FEATURE [App::FeaturePython] Joint259  label="Fixed"  # Assembly joint (typed FeaturePython)
  Activated = true
  AngleMax = 0
  AngleMin = 0
  Detach1 = false
  Detach2 = false
  Distance = 0
  Distance2 = 0
  EnableAngleMax = false
  EnableAngleMin = false
  EnableLengthMax = false
  EnableLengthMin = false
  JointType = 0 (Fixed)
  LengthMax = 0
  LengthMin = 0
  Placement1 = pos=(0,10.5,0) rot=(-0.57735,-0.57735,0.57735;4.18879rad)
  Placement2 = pos=(0,0,1.6) rot=(0,0,1;0rad)
  Reference1 = -> Assembly [WDS673_82227.Part__Feature001.Edge6,WDS673_82227.Part__Feature001.Edge6]
  Reference2 = -> Assembly [foot_fasteners.Link020.Link020_i1.Washer.Edge1,foot_fasteners.Link020.Link020_i1.Washer.Edge1]
FEATURE [App::FeaturePython] Joint260  label="Fixed"  # Assembly joint (typed FeaturePython)
  Activated = true
  AngleMax = 0
  AngleMin = 0
  Detach1 = false
  Detach2 = false
  Distance = 0
  Distance2 = 0
  EnableAngleMax = false
  EnableAngleMin = false
  EnableLengthMax = false
  EnableLengthMin = false
  JointType = 0 (Fixed)
  LengthMax = 0
  LengthMin = 0
  Placement1 = pos=(0,10.5,0) rot=(-0.57735,-0.57735,0.57735;4.18879rad)
  Placement2 = pos=(0,0,1.6) rot=(0,0,1;0rad)
  Reference1 = -> Assembly [WDS673_82226.Part__Feature001.Edge65,WDS673_82226.Part__Feature001.Edge65]
  Reference2 = -> Assembly [foot_fasteners.Link020.Link020_i2.Washer.Edge1,foot_fasteners.Link020.Link020_i2.Washer.Edge1]
FEATURE [App::FeaturePython] Joint261  label="Fixed"  # Assembly joint (typed FeaturePython)
  Activated = true
  AngleMax = 0
  AngleMin = 0
  Detach1 = false
  Detach2 = false
  Distance = 0
  Distance2 = 0
  EnableAngleMax = false
  EnableAngleMin = false
  EnableLengthMax = false
  EnableLengthMin = false
  JointType = 0 (Fixed)
  LengthMax = 0
  LengthMin = 0
  Placement1 = pos=(0,10.5,0) rot=(-0.57735,-0.57735,0.57735;4.18879rad)
  Placement2 = pos=(0,0,1.6) rot=(0,0,1;0rad)
  Reference1 = -> Assembly [WDS673_82225.Part__Feature001.Edge65,WDS673_82225.Part__Feature001.Edge65]
  Reference2 = -> Assembly [foot_fasteners.Link020.Link020_i3.Washer.Edge1,foot_fasteners.Link020.Link020_i3.Washer.Edge1]
FEATURE [App::Link] WDS8520_251  label="WDS8520-251"
  LinkPlacement = pos=(-50,239.5,819) rot=(1,0,0;1.5708rad)
  LinkedObject = -> <external mechanical COTS/WDS8520-251.FCStd>#Part__Feature
  Placement = pos=(-50,239.5,819) rot=(1,0,0;1.5708rad)
FEATURE [App::DocumentObjectGroup] Group003  label="Lid Handle"
  Group = -> [lid_handle_fastener_group001,lid_handle_fastener_group,WDS8520_251]
FEATURE [App::FeaturePython] Joint262  label="Fixed"  # Assembly joint (typed FeaturePython)
  Activated = true
  AngleMax = 0
  AngleMin = 0
  Detach1 = false
  Detach2 = false
  Distance = 0
  Distance2 = 0
  EnableAngleMax = false
  EnableAngleMin = false
  EnableLengthMax = false
  EnableLengthMin = false
  JointType = 0 (Fixed)
  LengthMax = 0
  LengthMin = 0
  Offset2 = pos=(0,0,0) rot=(0,0,-1;1.5708rad)
  Placement1 = pos=(0,0,0) rot=(0.57735,0.57735,-0.57735;2.0944rad)
  Placement2 = pos=(-50,-213,-50) rot=(-0.57735,0.57735,-0.57735;4.18879rad)
  Reference1 = -> Assembly [WDS8520_251.Edge21,WDS8520_251.Edge21]
  Reference2 = -> Assembly [lid_frame.Edge312,lid_frame.Edge312]
FEATURE [App::Link] WDS4213_601  label="WDS4213-601"
  LinkPlacement = pos=(213.7,-0.05,278.25) rot=(0.707107,0.707107,0;3.14159rad)
  LinkedObject = -> <external mechanical COTS/WDS4213-601.FCStd>#WDS4213_601
  Placement = pos=(213.7,-0.05,278.25) rot=(0.707107,0.707107,0;3.14159rad)
FEATURE [App::Link] WDS4213_602  label="WDS4213-601"
  LinkPlacement = pos=(-213.7,0.05,278.25) rot=(-0.707107,0.707107,0;3.14159rad)
  LinkedObject = -> <external mechanical COTS/WDS4213-601.FCStd>#WDS4213_601
  Placement = pos=(-213.7,0.05,278.25) rot=(-0.707107,0.707107,0;3.14159rad)
FEATURE [App::DocumentObjectGroup] Group002  label="Lifting Handles"
  Group = -> [_37DSS,_37DSS001,WDS4213_602,WDS4213_601]
FEATURE [App::FeaturePython] Joint263  label="Fixed"  # Assembly joint (typed FeaturePython)
  Activated = true
  AngleMax = 0
  AngleMin = 0
  Detach1 = false
  Detach2 = false
  Distance = 0
  Distance2 = 0
  EnableAngleMax = false
  EnableAngleMin = false
  EnableLengthMax = false
  EnableLengthMin = false
  JointType = 0 (Fixed)
  LengthMax = 0
  LengthMin = 0
  Offset2 = pos=(0,0,0) rot=(0,0,1;3.14159rad)
  Placement1 = pos=(-41.25,18.25,4e-16) rot=(0,0,1;0rad)
  Placement2 = pos=(-41.3,-1.5,156.5) rot=(-1,0,0;4.71239rad)
  Reference1 = -> Assembly [WDS4213_601.Part__Feature.Edge16,WDS4213_601.Part__Feature.Edge16]
  Reference2 = -> Assembly [OCT_UFPNL_CB.Edge31,OCT_UFPNL_CB.Edge31]
FEATURE [App::FeaturePython] Joint264  label="Fixed"  # Assembly joint (typed FeaturePython)
  Activated = true
  AngleMax = 0
  AngleMin = 0
  Detach1 = false
  Detach2 = false
  Distance = 0
  Distance2 = 0
  EnableAngleMax = false
  EnableAngleMin = false
  EnableLengthMax = false
  EnableLengthMin = false
  JointType = 0 (Fixed)
  LengthMax = 0
  LengthMin = 0
  Offset2 = pos=(0,0,0) rot=(0,0,1;3.14159rad)
  Placement1 = pos=(-41.25,18.25,4e-16) rot=(0,0,1;0rad)
  Placement2 = pos=(-41.3,-1.5,156.5) rot=(1,0,0;1.5708rad)
  Reference1 = -> Assembly [WDS4213_602.Part__Feature.Edge16,WDS4213_602.Part__Feature.Edge16]
  Reference2 = -> Assembly [OCT_UFPNL_CB001.Edge31,OCT_UFPNL_CB001.Edge31]
FEATURE [Assembly::JointGroup] Joints
  Group = -> [GroundedJoint,Joint087,Joint089,Joint091,Joint095,Joint097,Joint099,Joint125,Joint126,Joint127,Joint129,Joint130,Joint131,Joint147,Joint148,Joint149,Joint150,Joint151,Joint152,Joint153,Joint154,Joint155,Joint156,Joint157,Joint158,Joint159,Joint160,Joint161,Joint163,Joint172,Joint174,Joint175,Joint176,Joint177,Joint178,Joint179,Joint180,Joint182,Joint185,Joint186,Joint187,Joint188,Joint189,+44 more]
FEATURE [Assembly::BomObject] Bill_of_Materials
  cells = A1='Index; B1='Name; C1='Description; D1='File Name; E1='Quantity; A2='1; B2='OCT-LIDFR-AA; D2='<path> RAD/OCT-LIDFR-AA.FCStd; E2=1; A3='2; B3='hinge upper fasteners; D3='<path>; E3=4; A4='2.1; B4='M6-Washer; D4='<path>; E4=1; A5='2.2; B5='M6x16-Screw; D5='<path>; E5=1; A6='2.3; B6='M6-Washer; D6='<path>; E6=1; A7='2.4; B7='M6-Nut; D7='<path>; E7=1; A8='3; B8='hinge lower fasteners; D8='<path>; E8=4; A9='3.1; B9='M6-Washer; D9='<path>; E9=1; A10='3.2; B10='M6-Nut; D10='<path>; E10=1; A11='3.3; B11='M6-Washer; D11='<path>; E11=1; A12='3.4; B12='M6x16-Screw; D12='<path>; E12=1; A13='4; B13='637DSS; D13='<path> COTS/Protex 637DSS Handle Backing Plate Stainless Steel (Natural).FCStd; E13=2; A14='5; B14='lid handle fasteners; D14='<path>; E14=2; A15='5.1; B15='M6-Washer; D15='<path>; E15=1; A16='5.2; B16='M6x16-Screw; D16='<path>; E16=1; A17='6; B17='OCT-CHBRA-AC; D17='<path> RAD/OCT-CHBRA-AC.FCStd; E17=8; A18='7; B18='OCT-LFPNL-BA; D18='<path> RAD/OCT-LFPNL.FCStd; E18=1; A19='8; B19='OCT-LFPNL-AB; D19='<path> RAD/OCT-LFPNL.FCStd; E19=6; A20='9; B20='OCT-LFPNL-CA; D20='<path> RAD/OCT-LFPNL.FCStd; E20=1; A21='10; B21='OCT-UFPNL-AB; D21='<path> RAD/OCT-UFPNL.FCStd; E21=5; A22='11; B22='OCT-UFPNL-CB; D22='<path> RAD/OCT-UFPNL.FCStd; E22=2; A23='12; B23='OCT-UFPNL-BB; D23='<path> RAD/OCT-UFPNL.FCStd; E23=1; A24='13; B24='OCT-CPBRC-AA; D24='<path> RAD/OCT-CPBRC.FCStd; E24=7; A25='14; B25='OCT-CPBRC-BA; D25='<path> RAD/OCT-CPBRC.FCStd; E25=1; A26='15; B26='OCT-LBRAC-AA; D26='<path> RAD/OCT-LBRAC-AA.FCStd; E26=6; A27='16; B27='OCT-LBLOK-AB; D27='<path> RAD/OCT-LBLOK-AB.FCStd; E27=4; A28='17; B28='OCT-UBRAC-AA; D28='<path> RAD/OCT-UBRAC-AA.FCStd; E28=6; A29='18; B29='OCT-ULBLK-AB; D29='<path> RAD/OCT-ULBLK-AB.FCStd; E29=2; A30='19; B30='OCT-URBLK-AB; D30='<path> RAD/OCT-URBLK-AB.FCStd; E30=2; A31='20; B31='OCT-LDHNG-AA; D31='<path>; E31=1; A32='20.1; B32='OCT-LDHNG-AA; D32='<path> COTS/OCT-LDHNG-AA.FCStd; E32=1; A33='20.1.1; B33='outer half; D33='<path> COTS/OCT-LDHNG-AA.FCStd; E33=2; A34='20.1.2; B34='inner half; D34='<path> COTS/OCT-LDHNG-AA.FCStd; E34=2; A35='21; B35='OCT-FRPLB-AA; D35='<path> RAD/OCT-FRPLB-AA.FCStd; E35=1; A36='22; B36='OCT-FRPLC-AA; D36='<path> RAD/OCT-FRPLC-AA.FCStd; E36=1; A37='23; B37='OCT-CHTOP-AA; D37='<path> RAD/OCT-CHTOP-AA.FCStd; E37=1; A38='24; B38='foot fasteners; D38='<path>; E38=1; A39='24.1; B39='single foot; D39='<path>; E39=1; A40='24.1.1; B40='M8-Nut; D40='<path>; E40=1; A41='24.1.2; B41='M8-Washer; D41='<path>; E41=1; A42='24.1.3; B42='M8-Washer; D42='<path>; E42=1; A43='25; B43='lower panel block fasteners; D43='<path>; E43=1; A44='25.1; B44='lower panel block single; D44='<path>; E44=1; A45='25.1.1; B45='M4x10-Screw; D45='<path>; E45=1; A46='25.1.2; B46='M4-Washer; D46='<path>; E46=1; A47='26; B47='lower panel bracket fasteners; D47='<path>; E47=1; A48='26.1; B48='single fastener; D48='<path>; E48=1; A49='26.1.1; B49='M4-Nut; D49='<path>; E49=1; A50='26.1.2; B50='M4-Washer; D50='<path>; +249 more cells
  columnsNames = Index | Name | Description | File Name | Quantity
  detailParts = true
  detailSubAssemblies = true
  onlyParts = false
FEATURE [Assembly::BomGroup] Bills_of_Materials
  Group = -> [Bill_of_Materials]
FEATURE [Assembly::AssemblyObject] Assembly  label="OCT-FRAME-A"
  Group = -> [Joints,Joint087,Joint089,Joint091,Joint095,Joint097,Joint099,Joint125,Joint126,Joint127,Joint129,Joint130,Joint131,Joint147,Joint148,Joint149,Joint150,Joint151,Joint152,Joint153,Joint154,Joint155,Joint156,Joint157,Joint158,Joint159,Joint160,Joint161,Joint163,Joint172,Joint174,Joint175,Joint176,Joint177,Joint178,Joint179,Joint180,Joint182,Joint185,Joint186,Joint187,Joint188,Joint189,Joint190,+146 more]
  Origin = -> Origin
  Type = Assembly
note: 49 file-system paths scrubbed to <path> (originals preserved in the JSON sidecar)
